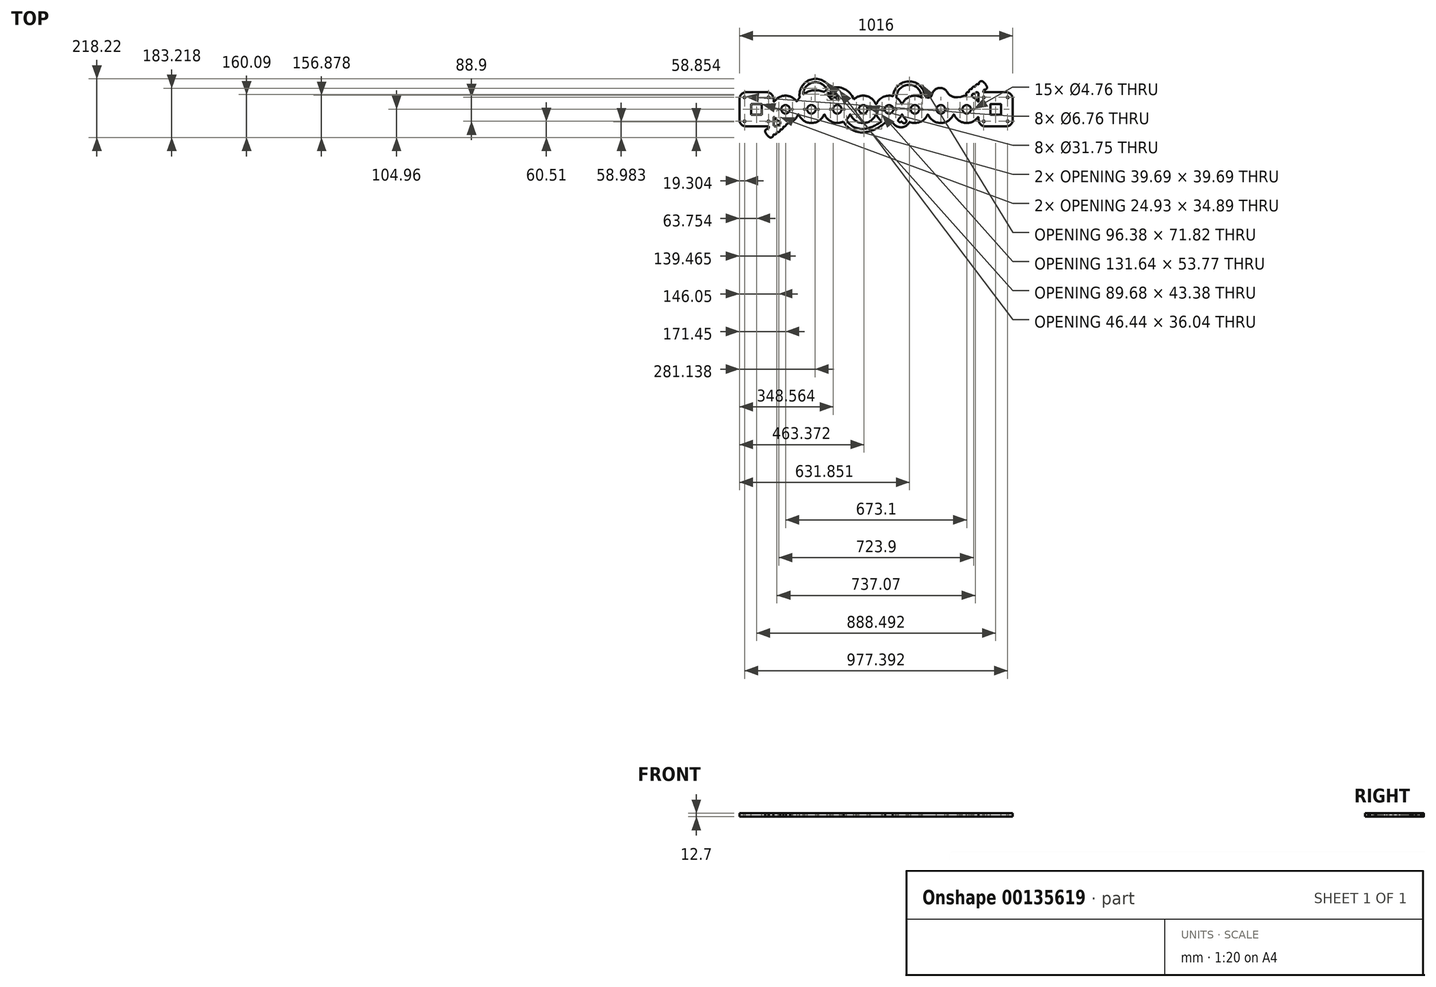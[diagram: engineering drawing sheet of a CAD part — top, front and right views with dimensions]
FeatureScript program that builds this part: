
annotation { "Feature Type Name" : "Feature", "Feature Type Description" : "" }
export const myFeature = defineFeature(function(context is Context, id is Id, definition is map)
    precondition{}
    {
        {
            var Q0;
            Q0=qCreatedBy(makeId("Top.planeOp"),FACE);
            var sketch = newSketch(context, id + "F0", { "sketchPlane" : qUnion([Q0])});
            skLineSegment(sketch, "E0", {"start": v(0, 0) * mm, "end": v(0, 330.74) * mm, "construction": true});
            skLineSegment(sketch, "E1.bottom", {"start": v(508, 63.5) * mm, "end": v(381, 63.5) * mm});
            skLineSegment(sketch, "E1.top", {"start": v(508, -63.5) * mm, "end": v(381, -63.5) * mm});
            skLineSegment(sketch, "E1.left", {"start": v(508, 63.5) * mm, "end": v(508, -63.5) * mm});
            skLineSegment(sketch, "E1.right", {"start": v(381, 63.5) * mm, "end": v(381, -63.5) * mm});
            skPoint(sketch, "E1.middle", {"position": v(444.5, 0) * mm});
            skPoint(sketch, "E2.MirrorP", {"position": v(-444.5, 0) * mm});
            skLineSegment(sketch, "E3.MirrorCS", {"start": v(-381, 63.5) * mm, "end": v(-381, -63.5) * mm});
            skLineSegment(sketch, "E4.MirrorCS", {"start": v(-508, 63.5) * mm, "end": v(-508, -63.5) * mm});
            skLineSegment(sketch, "E5.MirrorCS", {"start": v(-508, -63.5) * mm, "end": v(-381, -63.5) * mm});
            skLineSegment(sketch, "E6.MirrorCS", {"start": v(-508, 63.5) * mm, "end": v(-381, 63.5) * mm});
            skLineSegment(sketch, "E7", {"start": v(0, 0) * mm, "end": v(126.8, 0) * mm, "construction": true});
            skLineSegment(sketch, "E8.direction2", {"start": v(-381, -63.5) * mm, "end": v(-381, 63.5) * mm, "construction": true});
            skCircle(sketch, "E9", {"center": v(-336.55, 0) * mm, "radius": 50.8 * mm});
            skCircle(sketch, "E10.1.0.0", {"center": v(-240.4, 0) * mm, "radius": 50.8 * mm});
            skCircle(sketch, "E10.2.0.0", {"center": v(-144.24, 0) * mm, "radius": 50.8 * mm});
            skCircle(sketch, "E10.3.0.0", {"center": v(-48.08, 0) * mm, "radius": 50.8 * mm});
            skCircle(sketch, "E10.4.0.0", {"center": v(48.08, 0) * mm, "radius": 50.8 * mm});
            skCircle(sketch, "E10.5.0.0", {"center": v(144.24, 0) * mm, "radius": 50.8 * mm});
            skCircle(sketch, "E10.6.0.0", {"center": v(240.4, 0) * mm, "radius": 50.8 * mm});
            skCircle(sketch, "E10.7.0.0", {"center": v(336.55, 0) * mm, "radius": 50.8 * mm});
            skLineSegment(sketch, "E10.direction1", {"start": v(-336.55, 0) * mm, "end": v(-240.4, 0) * mm, "construction": true});
            skLineSegment(sketch, "E11", {"start": v(-381, 0) * mm, "end": v(-387.35, 0) * mm});
            skLineSegment(sketch, "E12", {"start": v(381, 0) * mm, "end": v(387.35, 0) * mm});
            skSolve(sketch);
        }
        {
            var Q0;
            Q0=qSketchRegion(id+"F0",true);
            extrude(context, id + "F1", {"entities" : qUnion([Q0]), "endBound" : BoundingType.SYMMETRIC, "depth" : 12.7 * mm});
        }
        {
            var Q0;
            Q0=makeQuery(id+"F1.opExtrude","SWEPT_EDGE",EDGE,{"disambiguationData":[OSD([sQuery(id+"F0.wireOp",EDGE,"E1.top"),sQuery(id+"F0.wireOp",EDGE,"E1.left")])]});
            var Q1;
            Q1=makeQuery(id+"F1.opExtrude","SWEPT_EDGE",EDGE,{"disambiguationData":[OSD([sQuery(id+"F0.wireOp",EDGE,"E1.top"),sQuery(id+"F0.wireOp",EDGE,"E1.right")])]});
            var Q2;
            Q2=makeQuery(id+"F1.opExtrude","SWEPT_EDGE",EDGE,{"disambiguationData":[OSD([sQuery(id+"F0.wireOp",EDGE,"E1.bottom"),sQuery(id+"F0.wireOp",EDGE,"E1.left")])]});
            var Q3;
            Q3=makeQuery(id+"F1.opExtrude","SWEPT_EDGE",EDGE,{"disambiguationData":[OSD([sQuery(id+"F0.wireOp",EDGE,"E4.MirrorCS"),sQuery(id+"F0.wireOp",EDGE,"E5.MirrorCS")])]});
            var Q4;
            Q4=makeQuery(id+"F1.opExtrude","SWEPT_EDGE",EDGE,{"disambiguationData":[OSD([sQuery(id+"F0.wireOp",EDGE,"E4.MirrorCS"),sQuery(id+"F0.wireOp",EDGE,"E6.MirrorCS")])]});
            var Q5;
            Q5=makeQuery(id+"F1.opExtrude","SWEPT_EDGE",EDGE,{"disambiguationData":[OSD([sQuery(id+"F0.wireOp",EDGE,"E3.MirrorCS"),sQuery(id+"F0.wireOp",EDGE,"E6.MirrorCS")])]});
            fillet(context, id + "F2", {"entities" : qUnion([Q0, Q1, Q2, Q3, Q4, Q5]), "radius" : 25.4 * mm, "tangentPropagation" : true, "allowEdgeOverflow" : false});
        }
        {
            var Q0;
            Q0=makeQuery(id+"F1.opExtrude","CAP_FACE",FACE,{"disambiguationData":[OSD([sQuery(id+"F0.wireOp",EDGE,"E1.bottom"),sQuery(id+"F0.wireOp",EDGE,"E1.top"),sQuery(id+"F0.wireOp",EDGE,"E1.left"),sQuery(id+"F0.wireOp",EDGE,"E1.right"),sQuery(id+"F0.wireOp",EDGE,"E3.MirrorCS"),sQuery(id+"F0.wireOp",EDGE,"E4.MirrorCS"),sQuery(id+"F0.wireOp",EDGE,"E5.MirrorCS"),sQuery(id+"F0.wireOp",EDGE,"E6.MirrorCS"),sQuery(id+"F0.wireOp",EDGE,"E9"),sQuery(id+"F0.wireOp",EDGE,"E10.1.0.0"),sQuery(id+"F0.wireOp",EDGE,"E10.2.0.0"),sQuery(id+"F0.wireOp",EDGE,"E10.3.0.0"),sQuery(id+"F0.wireOp",EDGE,"E10.4.0.0"),sQuery(id+"F0.wireOp",EDGE,"E10.5.0.0"),sQuery(id+"F0.wireOp",EDGE,"E10.6.0.0"),sQuery(id+"F0.wireOp",EDGE,"E10.7.0.0")])],"isStart":false});
            var sketch = newSketch(context, id + "F3", { "sketchPlane" : qUnion([Q0])});
            skArc(sketch, "E13", {"start": v(-381, -56.63) * mm, "mid": v(-374.13, -63.5) * mm, "end": v(-367.26, -56.63) * mm});
            skArc(sketch, "E14", {"start": v(-367.26, -56.63) * mm, "mid": v(-357.18, -55.03) * mm, "end": v(-359.8, -45.17) * mm});
            skArc(sketch, "E15", {"start": v(-347.92, -61.66) * mm, "mid": v(-336.63, -61.98) * mm, "end": v(-338.08, -50.78) * mm});
            skArc(sketch, "E16", {"start": v(-359.38, -71.23) * mm, "mid": v(-347.9, -73.34) * mm, "end": v(-347.92, -61.66) * mm});
            skArc(sketch, "E17", {"start": v(-369.91, -80.78) * mm, "mid": v(-358.7, -82.57) * mm, "end": v(-359.38, -71.23) * mm});
            skArc(sketch, "E18", {"start": v(-383, -91.32) * mm, "mid": v(-371.86, -91.75) * mm, "end": v(-369.91, -80.78) * mm});
            skArc(sketch, "E19", {"start": v(-397.93, -102.36) * mm, "mid": v(-385.83, -103.1) * mm, "end": v(-383, -91.32) * mm});
            skArc(sketch, "E20", {"start": v(-411.58, -84.76) * mm, "mid": v(-405.65, -94.26) * mm, "end": v(-397.93, -102.36) * mm});
            skArc(sketch, "E21", {"start": v(-399.42, -73.2) * mm, "mid": v(-409.27, -75) * mm, "end": v(-411.58, -84.76) * mm});
            skArc(sketch, "E22.0", {"start": v(-359.8, -45.17) * mm, "mid": v(-349.25, -49.19) * mm, "end": v(-338.08, -50.78) * mm});
            skLineSegment(sketch, "E23.0", {"start": v(-381, -56.63) * mm, "end": v(-381, -63.5) * mm});
            skLineSegment(sketch, "E24.0", {"start": v(-401.54, -63.5) * mm, "end": v(-381, -63.5) * mm});
            skPoint(sketch, "E25.orphan", {"position": v(-381, -24.6) * mm});
            skPoint(sketch, "E26.orphan", {"position": v(-482.6, -63.5) * mm});
            skPoint(sketch, "E27.orphan", {"position": v(-288.47, -16.4) * mm});
            skArc(sketch, "E28", {"start": v(-388.23, -65.24) * mm, "mid": v(-397.09, -64.64) * mm, "end": v(-399.42, -73.2) * mm});
            skCircle(sketch, "E29", {"center": v(0, 0) * mm, "radius": 77.09 * mm, "construction": true});
            skPoint(sketch, "E30.1.0", {"position": v(288.47, 16.4) * mm});
            skPoint(sketch, "E30.1.1", {"position": v(381, 24.6) * mm});
            skArc(sketch, "E30.1.2", {"start": v(383, 91.32) * mm, "mid": v(371.86, 91.75) * mm, "end": v(369.91, 80.78) * mm});
            skArc(sketch, "E30.1.3", {"start": v(359.38, 71.23) * mm, "mid": v(347.9, 73.34) * mm, "end": v(347.92, 61.66) * mm});
            skArc(sketch, "E30.1.4", {"start": v(347.92, 61.66) * mm, "mid": v(336.63, 61.98) * mm, "end": v(338.08, 50.78) * mm});
            skArc(sketch, "E30.1.5", {"start": v(397.93, 102.36) * mm, "mid": v(385.83, 103.1) * mm, "end": v(383, 91.32) * mm});
            skArc(sketch, "E30.1.6", {"start": v(411.58, 84.76) * mm, "mid": v(405.65, 94.26) * mm, "end": v(397.93, 102.36) * mm});
            skArc(sketch, "E30.1.7", {"start": v(359.8, 45.17) * mm, "mid": v(349.25, 49.19) * mm, "end": v(338.08, 50.78) * mm});
            skArc(sketch, "E30.1.8", {"start": v(369.91, 80.78) * mm, "mid": v(358.7, 82.57) * mm, "end": v(359.38, 71.23) * mm});
            skArc(sketch, "E30.1.9", {"start": v(367.26, 56.63) * mm, "mid": v(357.18, 55.03) * mm, "end": v(359.8, 45.17) * mm});
            skArc(sketch, "E30.1.10", {"start": v(399.42, 73.2) * mm, "mid": v(409.27, 75) * mm, "end": v(411.58, 84.76) * mm});
            skLineSegment(sketch, "E30.1.11", {"start": v(401.54, 63.5) * mm, "end": v(381, 63.5) * mm});
            skArc(sketch, "E30.1.12", {"start": v(388.23, 65.24) * mm, "mid": v(397.09, 64.64) * mm, "end": v(399.42, 73.2) * mm});
            skLineSegment(sketch, "E30.1.13", {"start": v(381, 56.63) * mm, "end": v(381, 63.5) * mm});
            skArc(sketch, "E30.1.14", {"start": v(381, 56.63) * mm, "mid": v(374.13, 63.5) * mm, "end": v(367.26, 56.63) * mm});
            skSolve(sketch);
        }
        {
            var Q0;
            Q0 = qSketchRegion(id + "F3", true);
            var Q1;
            Q1=makeQuery(id+"F1.opExtrude","CAP_FACE",FACE,{"disambiguationData":[OSD([sQuery(id+"F0.wireOp",EDGE,"E1.bottom"),sQuery(id+"F0.wireOp",EDGE,"E1.top"),sQuery(id+"F0.wireOp",EDGE,"E1.left"),sQuery(id+"F0.wireOp",EDGE,"E1.right"),sQuery(id+"F0.wireOp",EDGE,"E3.MirrorCS"),sQuery(id+"F0.wireOp",EDGE,"E4.MirrorCS"),sQuery(id+"F0.wireOp",EDGE,"E5.MirrorCS"),sQuery(id+"F0.wireOp",EDGE,"E6.MirrorCS"),sQuery(id+"F0.wireOp",EDGE,"E9"),sQuery(id+"F0.wireOp",EDGE,"E10.1.0.0"),sQuery(id+"F0.wireOp",EDGE,"E10.2.0.0"),sQuery(id+"F0.wireOp",EDGE,"E10.3.0.0"),sQuery(id+"F0.wireOp",EDGE,"E10.4.0.0"),sQuery(id+"F0.wireOp",EDGE,"E10.5.0.0"),sQuery(id+"F0.wireOp",EDGE,"E10.6.0.0"),sQuery(id+"F0.wireOp",EDGE,"E10.7.0.0")])],"isStart":true});
            extrude(context, id + "F4", {"entities" : qUnion([Q0]), "operationType" : NewBodyOperationType.ADD, "endBound" : BoundingType.UP_TO_SURFACE, "oppositeDirection" : true, "endBoundEntityFace" : qUnion([Q1]), "depth" : 25.4 * mm});
        }
        {
            var Q0;
            Q0=makeQuery(id+"F4.boolean.opBoolean","MERGE",FACE,{"derivedFrom":[makeQuery(id+"F1.opExtrude","CAP_FACE",FACE,{"disambiguationData":[OSD([sQuery(id+"F0.wireOp",EDGE,"E1.bottom"),sQuery(id+"F0.wireOp",EDGE,"E1.top"),sQuery(id+"F0.wireOp",EDGE,"E1.left"),sQuery(id+"F0.wireOp",EDGE,"E1.right"),sQuery(id+"F0.wireOp",EDGE,"E3.MirrorCS"),sQuery(id+"F0.wireOp",EDGE,"E4.MirrorCS"),sQuery(id+"F0.wireOp",EDGE,"E5.MirrorCS"),sQuery(id+"F0.wireOp",EDGE,"E6.MirrorCS"),sQuery(id+"F0.wireOp",EDGE,"E9"),sQuery(id+"F0.wireOp",EDGE,"E10.1.0.0"),sQuery(id+"F0.wireOp",EDGE,"E10.2.0.0"),sQuery(id+"F0.wireOp",EDGE,"E10.3.0.0"),sQuery(id+"F0.wireOp",EDGE,"E10.4.0.0"),sQuery(id+"F0.wireOp",EDGE,"E10.5.0.0"),sQuery(id+"F0.wireOp",EDGE,"E10.6.0.0"),sQuery(id+"F0.wireOp",EDGE,"E10.7.0.0")])],"isStart":false}),makeQuery(id+"F4.opExtrude","CAP_FACE",FACE,{"disambiguationData":[OSD([sQuery(id+"F3.wireOp",EDGE,"E13"),sQuery(id+"F3.wireOp",EDGE,"E14"),sQuery(id+"F3.wireOp",EDGE,"E15"),sQuery(id+"F3.wireOp",EDGE,"E16"),sQuery(id+"F3.wireOp",EDGE,"E17"),sQuery(id+"F3.wireOp",EDGE,"E18"),sQuery(id+"F3.wireOp",EDGE,"E19"),sQuery(id+"F3.wireOp",EDGE,"E20"),sQuery(id+"F3.wireOp",EDGE,"E21"),sQuery(id+"F3.wireOp",EDGE,"E22.0"),sQuery(id+"F3.wireOp",EDGE,"E23.0"),sQuery(id+"F3.wireOp",EDGE,"E24.0"),sQuery(id+"F3.wireOp",EDGE,"E28")])],"isStart":true}),makeQuery(id+"F4.opExtrude","CAP_FACE",FACE,{"disambiguationData":[OSD([sQuery(id+"F3.wireOp",EDGE,"E30.1.2"),sQuery(id+"F3.wireOp",EDGE,"E30.1.3"),sQuery(id+"F3.wireOp",EDGE,"E30.1.4"),sQuery(id+"F3.wireOp",EDGE,"E30.1.5"),sQuery(id+"F3.wireOp",EDGE,"E30.1.6"),sQuery(id+"F3.wireOp",EDGE,"E30.1.7"),sQuery(id+"F3.wireOp",EDGE,"E30.1.8"),sQuery(id+"F3.wireOp",EDGE,"E30.1.9"),sQuery(id+"F3.wireOp",EDGE,"E30.1.10"),sQuery(id+"F3.wireOp",EDGE,"E30.1.11"),sQuery(id+"F3.wireOp",EDGE,"E30.1.12"),sQuery(id+"F3.wireOp",EDGE,"E30.1.13"),sQuery(id+"F3.wireOp",EDGE,"E30.1.14")])],"isStart":true})]});
            var sketch = newSketch(context, id + "F5", { "sketchPlane" : qUnion([Q0])});
            skArc(sketch, "E31", {"start": v(-82.98, 36.91) * mm, "mid": v(-130.84, 79.98) * mm, "end": v(-193.32, 64.4) * mm});
            skArc(sketch, "E32", {"start": v(-193.32, 64.4) * mm, "mid": v(-250.9, 66.18) * mm, "end": v(-294.48, 28.47) * mm});
            skArc(sketch, "E33.0", {"start": v(-96.16, 16.4) * mm, "mid": v(-144.24, 50.8) * mm, "end": v(-192.31, 16.4) * mm});
            skArc(sketch, "E34.0", {"start": v(-192.31, 16.4) * mm, "mid": v(-240.4, 50.8) * mm, "end": v(-288.47, 16.4) * mm});
            skArc(sketch, "E35.0", {"start": v(-82.98, 36.91) * mm, "mid": v(-90.82, 27.46) * mm, "end": v(-96.16, 16.4) * mm});
            skArc(sketch, "E36.0", {"start": v(-288.47, 16.4) * mm, "mid": v(-291.07, 22.64) * mm, "end": v(-294.48, 28.47) * mm});
            skPoint(sketch, "E37.orphan", {"position": v(0, 16.4) * mm});
            skPoint(sketch, "E38.orphan", {"position": v(-381, 24.6) * mm});
            skSolve(sketch);
        }
        {
            var Q0;
            Q0 = qSketchRegion(id + "F5", true);
            var Q1;
            {var subQ0=sQuery(id+"F0.wireOp",EDGE,"E10.7.0.0");var subQ1=sQuery(id+"F0.wireOp",EDGE,"E10.6.0.0");var subQ2=sQuery(id+"F0.wireOp",EDGE,"E10.5.0.0");var subQ3=sQuery(id+"F0.wireOp",EDGE,"E10.4.0.0");var subQ4=sQuery(id+"F0.wireOp",EDGE,"E10.3.0.0");var subQ5=sQuery(id+"F0.wireOp",EDGE,"E10.2.0.0");var subQ6=sQuery(id+"F0.wireOp",EDGE,"E10.1.0.0");var subQ7=sQuery(id+"F0.wireOp",EDGE,"E9");var subQ8=sQuery(id+"F0.wireOp",EDGE,"E6.MirrorCS");var subQ9=sQuery(id+"F0.wireOp",EDGE,"E5.MirrorCS");var subQ10=sQuery(id+"F0.wireOp",EDGE,"E4.MirrorCS");var subQ11=sQuery(id+"F0.wireOp",EDGE,"E3.MirrorCS");var subQ12=sQuery(id+"F0.wireOp",EDGE,"E1.right");var subQ13=sQuery(id+"F0.wireOp",EDGE,"E1.left");var subQ14=sQuery(id+"F0.wireOp",EDGE,"E1.top");var subQ15=sQuery(id+"F0.wireOp",EDGE,"E1.bottom");Q1=makeQuery(id+"F4.boolean.opBoolean","MERGE",FACE,{"derivedFrom":[makeQuery(id+"F1.opExtrude","CAP_FACE",FACE,{"disambiguationData":[OSD([subQ15,subQ14,subQ13,subQ12,subQ11,subQ10,subQ9,subQ8,subQ7,subQ6,subQ5,subQ4,subQ3,subQ2,subQ1,subQ0])],"isStart":true}),makeQuery(id+"F4.opExtrude","CAP_FACE",FACE,{"disambiguationData":[OSD([subQ15,subQ14,subQ13,subQ12,subQ11,subQ10,subQ9,subQ8,subQ7,subQ6,subQ5,subQ4,subQ3,subQ2,subQ1,subQ0]),ownerDisambiguation([makeQuery(id+"F4.opExtrude","SWEPT_BODY",BODY,{"disambiguationData":[OSD([sQuery(id+"F3.wireOp",EDGE,"E13"),sQuery(id+"F3.wireOp",EDGE,"E14"),sQuery(id+"F3.wireOp",EDGE,"E15"),sQuery(id+"F3.wireOp",EDGE,"E16"),sQuery(id+"F3.wireOp",EDGE,"E17"),sQuery(id+"F3.wireOp",EDGE,"E18"),sQuery(id+"F3.wireOp",EDGE,"E19"),sQuery(id+"F3.wireOp",EDGE,"E20"),sQuery(id+"F3.wireOp",EDGE,"E21"),sQuery(id+"F3.wireOp",EDGE,"E22.0"),sQuery(id+"F3.wireOp",EDGE,"E23.0"),sQuery(id+"F3.wireOp",EDGE,"E24.0"),sQuery(id+"F3.wireOp",EDGE,"E28")])]})])],"isStart":false}),makeQuery(id+"F4.opExtrude","CAP_FACE",FACE,{"disambiguationData":[OSD([subQ15,subQ14,subQ13,subQ12,subQ11,subQ10,subQ9,subQ8,subQ7,subQ6,subQ5,subQ4,subQ3,subQ2,subQ1,subQ0]),ownerDisambiguation([makeQuery(id+"F4.opExtrude","SWEPT_BODY",BODY,{"disambiguationData":[OSD([sQuery(id+"F3.wireOp",EDGE,"E30.1.2"),sQuery(id+"F3.wireOp",EDGE,"E30.1.3"),sQuery(id+"F3.wireOp",EDGE,"E30.1.4"),sQuery(id+"F3.wireOp",EDGE,"E30.1.5"),sQuery(id+"F3.wireOp",EDGE,"E30.1.6"),sQuery(id+"F3.wireOp",EDGE,"E30.1.7"),sQuery(id+"F3.wireOp",EDGE,"E30.1.8"),sQuery(id+"F3.wireOp",EDGE,"E30.1.9"),sQuery(id+"F3.wireOp",EDGE,"E30.1.10"),sQuery(id+"F3.wireOp",EDGE,"E30.1.11"),sQuery(id+"F3.wireOp",EDGE,"E30.1.12"),sQuery(id+"F3.wireOp",EDGE,"E30.1.13"),sQuery(id+"F3.wireOp",EDGE,"E30.1.14")])]})])],"isStart":false})]});}
            extrude(context, id + "F6", {"entities" : qUnion([Q0]), "operationType" : NewBodyOperationType.ADD, "endBound" : BoundingType.UP_TO_SURFACE, "oppositeDirection" : true, "endBoundEntityFace" : qUnion([Q1]), "depth" : 25.4 * mm});
        }
        {
            var Q0;
            Q0=makeQuery(id+"F6.boolean.opBoolean","MERGE",FACE,{"derivedFrom":[makeQuery(id+"F4.boolean.opBoolean","MERGE",FACE,{"derivedFrom":[makeQuery(id+"F1.opExtrude","CAP_FACE",FACE,{"disambiguationData":[OSD([sQuery(id+"F0.wireOp",EDGE,"E1.bottom"),sQuery(id+"F0.wireOp",EDGE,"E1.top"),sQuery(id+"F0.wireOp",EDGE,"E1.left"),sQuery(id+"F0.wireOp",EDGE,"E1.right"),sQuery(id+"F0.wireOp",EDGE,"E3.MirrorCS"),sQuery(id+"F0.wireOp",EDGE,"E4.MirrorCS"),sQuery(id+"F0.wireOp",EDGE,"E5.MirrorCS"),sQuery(id+"F0.wireOp",EDGE,"E6.MirrorCS"),sQuery(id+"F0.wireOp",EDGE,"E9"),sQuery(id+"F0.wireOp",EDGE,"E10.1.0.0"),sQuery(id+"F0.wireOp",EDGE,"E10.2.0.0"),sQuery(id+"F0.wireOp",EDGE,"E10.3.0.0"),sQuery(id+"F0.wireOp",EDGE,"E10.4.0.0"),sQuery(id+"F0.wireOp",EDGE,"E10.5.0.0"),sQuery(id+"F0.wireOp",EDGE,"E10.6.0.0"),sQuery(id+"F0.wireOp",EDGE,"E10.7.0.0")])],"isStart":false}),makeQuery(id+"F4.opExtrude","CAP_FACE",FACE,{"disambiguationData":[OSD([sQuery(id+"F3.wireOp",EDGE,"E13"),sQuery(id+"F3.wireOp",EDGE,"E14"),sQuery(id+"F3.wireOp",EDGE,"E15"),sQuery(id+"F3.wireOp",EDGE,"E16"),sQuery(id+"F3.wireOp",EDGE,"E17"),sQuery(id+"F3.wireOp",EDGE,"E18"),sQuery(id+"F3.wireOp",EDGE,"E19"),sQuery(id+"F3.wireOp",EDGE,"E20"),sQuery(id+"F3.wireOp",EDGE,"E21"),sQuery(id+"F3.wireOp",EDGE,"E22.0"),sQuery(id+"F3.wireOp",EDGE,"E23.0"),sQuery(id+"F3.wireOp",EDGE,"E24.0"),sQuery(id+"F3.wireOp",EDGE,"E28")])],"isStart":true}),makeQuery(id+"F4.opExtrude","CAP_FACE",FACE,{"disambiguationData":[OSD([sQuery(id+"F3.wireOp",EDGE,"E30.1.2"),sQuery(id+"F3.wireOp",EDGE,"E30.1.3"),sQuery(id+"F3.wireOp",EDGE,"E30.1.4"),sQuery(id+"F3.wireOp",EDGE,"E30.1.5"),sQuery(id+"F3.wireOp",EDGE,"E30.1.6"),sQuery(id+"F3.wireOp",EDGE,"E30.1.7"),sQuery(id+"F3.wireOp",EDGE,"E30.1.8"),sQuery(id+"F3.wireOp",EDGE,"E30.1.9"),sQuery(id+"F3.wireOp",EDGE,"E30.1.10"),sQuery(id+"F3.wireOp",EDGE,"E30.1.11"),sQuery(id+"F3.wireOp",EDGE,"E30.1.12"),sQuery(id+"F3.wireOp",EDGE,"E30.1.13"),sQuery(id+"F3.wireOp",EDGE,"E30.1.14")])],"isStart":true})]}),makeQuery(id+"F6.opExtrude","CAP_FACE",FACE,{"disambiguationData":[OSD([sQuery(id+"F5.wireOp",EDGE,"E31"),sQuery(id+"F5.wireOp",EDGE,"E32"),sQuery(id+"F5.wireOp",EDGE,"E33.0"),sQuery(id+"F5.wireOp",EDGE,"E34.0"),sQuery(id+"F5.wireOp",EDGE,"E35.0"),sQuery(id+"F5.wireOp",EDGE,"E36.0")])],"isStart":true})]});
            var sketch = newSketch(context, id + "F7", { "sketchPlane" : qUnion([Q0])});
            skArc(sketch, "E39", {"start": v(84.14, -35.78) * mm, "mid": v(85.22, -46.67) * mm, "end": v(95.4, -42.66) * mm});
            skArc(sketch, "E40", {"start": v(95.4, -42.66) * mm, "mid": v(105.84, -51.57) * mm, "end": v(112.13, -39.37) * mm});
            skArc(sketch, "E41", {"start": v(61.74, -48.93) * mm, "mid": v(93.64, -66.78) * mm, "end": v(124.18, -46.67) * mm});
            skPoint(sketch, "E41.endSnap0", {"position": v(85.22, -46.67) * mm});
            skArc(sketch, "E42.0", {"start": v(61.74, -48.93) * mm, "mid": v(73.8, -43.81) * mm, "end": v(84.14, -35.78) * mm});
            skPoint(sketch, "E43.orphan", {"position": v(0, -16.4) * mm});
            skPoint(sketch, "E44.orphan", {"position": v(192.31, -16.4) * mm});
            skPoint(sketch, "E45.orphan", {"position": v(96.16, -16.4) * mm});
            skSolve(sketch);
        }
        {
            var Q0;
            Q0 = qSketchRegion(id + "F7", true);
            var Q1;
            {var subQ0=sQuery(id+"F7.wireOp",EDGE,"E40");Q1=makeQuery(id+"F7.imprint","IMPRINT",FACE,{"disambiguationData":[TD([[makeQuery(id+"F7.imprint","IMPRINT",EDGE,{"derivedFrom":subQ0}),-1.0]])]});}
            var Q2;
            {var subQ0=sQuery(id+"F0.wireOp",EDGE,"E10.7.0.0");var subQ1=sQuery(id+"F0.wireOp",EDGE,"E10.6.0.0");var subQ2=sQuery(id+"F0.wireOp",EDGE,"E10.5.0.0");var subQ3=sQuery(id+"F0.wireOp",EDGE,"E10.4.0.0");var subQ4=sQuery(id+"F0.wireOp",EDGE,"E10.3.0.0");var subQ5=sQuery(id+"F0.wireOp",EDGE,"E10.2.0.0");var subQ6=sQuery(id+"F0.wireOp",EDGE,"E10.1.0.0");var subQ7=sQuery(id+"F0.wireOp",EDGE,"E9");var subQ8=sQuery(id+"F0.wireOp",EDGE,"E6.MirrorCS");var subQ9=sQuery(id+"F0.wireOp",EDGE,"E5.MirrorCS");var subQ10=sQuery(id+"F0.wireOp",EDGE,"E4.MirrorCS");var subQ11=sQuery(id+"F0.wireOp",EDGE,"E3.MirrorCS");var subQ12=sQuery(id+"F0.wireOp",EDGE,"E1.right");var subQ13=sQuery(id+"F0.wireOp",EDGE,"E1.left");var subQ14=sQuery(id+"F0.wireOp",EDGE,"E1.top");var subQ15=sQuery(id+"F0.wireOp",EDGE,"E1.bottom");Q2=makeQuery(id+"F6.boolean.opBoolean","MERGE",FACE,{"derivedFrom":[makeQuery(id+"F4.boolean.opBoolean","MERGE",FACE,{"derivedFrom":[makeQuery(id+"F1.opExtrude","CAP_FACE",FACE,{"disambiguationData":[OSD([subQ15,subQ14,subQ13,subQ12,subQ11,subQ10,subQ9,subQ8,subQ7,subQ6,subQ5,subQ4,subQ3,subQ2,subQ1,subQ0])],"isStart":true}),makeQuery(id+"F4.opExtrude","CAP_FACE",FACE,{"disambiguationData":[OSD([subQ15,subQ14,subQ13,subQ12,subQ11,subQ10,subQ9,subQ8,subQ7,subQ6,subQ5,subQ4,subQ3,subQ2,subQ1,subQ0]),ownerDisambiguation([makeQuery(id+"F4.opExtrude","SWEPT_BODY",BODY,{"disambiguationData":[OSD([sQuery(id+"F3.wireOp",EDGE,"E13"),sQuery(id+"F3.wireOp",EDGE,"E14"),sQuery(id+"F3.wireOp",EDGE,"E15"),sQuery(id+"F3.wireOp",EDGE,"E16"),sQuery(id+"F3.wireOp",EDGE,"E17"),sQuery(id+"F3.wireOp",EDGE,"E18"),sQuery(id+"F3.wireOp",EDGE,"E19"),sQuery(id+"F3.wireOp",EDGE,"E20"),sQuery(id+"F3.wireOp",EDGE,"E21"),sQuery(id+"F3.wireOp",EDGE,"E22.0"),sQuery(id+"F3.wireOp",EDGE,"E23.0"),sQuery(id+"F3.wireOp",EDGE,"E24.0"),sQuery(id+"F3.wireOp",EDGE,"E28")])]})])],"isStart":false}),makeQuery(id+"F4.opExtrude","CAP_FACE",FACE,{"disambiguationData":[OSD([subQ15,subQ14,subQ13,subQ12,subQ11,subQ10,subQ9,subQ8,subQ7,subQ6,subQ5,subQ4,subQ3,subQ2,subQ1,subQ0]),ownerDisambiguation([makeQuery(id+"F4.opExtrude","SWEPT_BODY",BODY,{"disambiguationData":[OSD([sQuery(id+"F3.wireOp",EDGE,"E30.1.2"),sQuery(id+"F3.wireOp",EDGE,"E30.1.3"),sQuery(id+"F3.wireOp",EDGE,"E30.1.4"),sQuery(id+"F3.wireOp",EDGE,"E30.1.5"),sQuery(id+"F3.wireOp",EDGE,"E30.1.6"),sQuery(id+"F3.wireOp",EDGE,"E30.1.7"),sQuery(id+"F3.wireOp",EDGE,"E30.1.8"),sQuery(id+"F3.wireOp",EDGE,"E30.1.9"),sQuery(id+"F3.wireOp",EDGE,"E30.1.10"),sQuery(id+"F3.wireOp",EDGE,"E30.1.11"),sQuery(id+"F3.wireOp",EDGE,"E30.1.12"),sQuery(id+"F3.wireOp",EDGE,"E30.1.13"),sQuery(id+"F3.wireOp",EDGE,"E30.1.14")])]})])],"isStart":false})]}),makeQuery(id+"F6.opExtrude","CAP_FACE",FACE,{"disambiguationData":[OSD([subQ15,subQ14,subQ13,subQ12,subQ11,subQ10,subQ9,subQ8,subQ7,subQ6,subQ5,subQ4,subQ3,subQ2,subQ1,subQ0])],"isStart":false})]});}
            extrude(context, id + "F8", {"entities" : qUnion([Q0, Q1]), "operationType" : NewBodyOperationType.ADD, "endBound" : BoundingType.UP_TO_SURFACE, "oppositeDirection" : true, "endBoundEntityFace" : qUnion([Q2]), "depth" : 25.4 * mm});
        }
        {
            var Q0;
            {var subQ0=sQuery(id+"F0.wireOp",EDGE,"E10.5.0.0");Q0=makeQuery(id+"F8.boolean.opBoolean","MERGE",FACE,{"derivedFrom":[makeQuery(id+"F6.boolean.opBoolean","MERGE",FACE,{"derivedFrom":[makeQuery(id+"F4.boolean.opBoolean","MERGE",FACE,{"derivedFrom":[makeQuery(id+"F1.opExtrude","CAP_FACE",FACE,{"disambiguationData":[OSD([sQuery(id+"F0.wireOp",EDGE,"E1.bottom"),sQuery(id+"F0.wireOp",EDGE,"E1.top"),sQuery(id+"F0.wireOp",EDGE,"E1.left"),sQuery(id+"F0.wireOp",EDGE,"E1.right"),sQuery(id+"F0.wireOp",EDGE,"E3.MirrorCS"),sQuery(id+"F0.wireOp",EDGE,"E4.MirrorCS"),sQuery(id+"F0.wireOp",EDGE,"E5.MirrorCS"),sQuery(id+"F0.wireOp",EDGE,"E6.MirrorCS"),sQuery(id+"F0.wireOp",EDGE,"E9"),sQuery(id+"F0.wireOp",EDGE,"E10.1.0.0"),sQuery(id+"F0.wireOp",EDGE,"E10.2.0.0"),sQuery(id+"F0.wireOp",EDGE,"E10.3.0.0"),sQuery(id+"F0.wireOp",EDGE,"E10.4.0.0"),subQ0,sQuery(id+"F0.wireOp",EDGE,"E10.6.0.0"),sQuery(id+"F0.wireOp",EDGE,"E10.7.0.0")])],"isStart":false}),makeQuery(id+"F4.opExtrude","CAP_FACE",FACE,{"disambiguationData":[OSD([sQuery(id+"F3.wireOp",EDGE,"E13"),sQuery(id+"F3.wireOp",EDGE,"E14"),sQuery(id+"F3.wireOp",EDGE,"E15"),sQuery(id+"F3.wireOp",EDGE,"E16"),sQuery(id+"F3.wireOp",EDGE,"E17"),sQuery(id+"F3.wireOp",EDGE,"E18"),sQuery(id+"F3.wireOp",EDGE,"E19"),sQuery(id+"F3.wireOp",EDGE,"E20"),sQuery(id+"F3.wireOp",EDGE,"E21"),sQuery(id+"F3.wireOp",EDGE,"E22.0"),sQuery(id+"F3.wireOp",EDGE,"E23.0"),sQuery(id+"F3.wireOp",EDGE,"E24.0"),sQuery(id+"F3.wireOp",EDGE,"E28")])],"isStart":true}),makeQuery(id+"F4.opExtrude","CAP_FACE",FACE,{"disambiguationData":[OSD([sQuery(id+"F3.wireOp",EDGE,"E30.1.2"),sQuery(id+"F3.wireOp",EDGE,"E30.1.3"),sQuery(id+"F3.wireOp",EDGE,"E30.1.4"),sQuery(id+"F3.wireOp",EDGE,"E30.1.5"),sQuery(id+"F3.wireOp",EDGE,"E30.1.6"),sQuery(id+"F3.wireOp",EDGE,"E30.1.7"),sQuery(id+"F3.wireOp",EDGE,"E30.1.8"),sQuery(id+"F3.wireOp",EDGE,"E30.1.9"),sQuery(id+"F3.wireOp",EDGE,"E30.1.10"),sQuery(id+"F3.wireOp",EDGE,"E30.1.11"),sQuery(id+"F3.wireOp",EDGE,"E30.1.12"),sQuery(id+"F3.wireOp",EDGE,"E30.1.13"),sQuery(id+"F3.wireOp",EDGE,"E30.1.14")])],"isStart":true})]}),makeQuery(id+"F6.opExtrude","CAP_FACE",FACE,{"disambiguationData":[OSD([sQuery(id+"F5.wireOp",EDGE,"E31"),sQuery(id+"F5.wireOp",EDGE,"E32"),sQuery(id+"F5.wireOp",EDGE,"E33.0"),sQuery(id+"F5.wireOp",EDGE,"E34.0"),sQuery(id+"F5.wireOp",EDGE,"E35.0"),sQuery(id+"F5.wireOp",EDGE,"E36.0")])],"isStart":true})]}),makeQuery(id+"F8.opExtrude","CAP_FACE",FACE,{"disambiguationData":[OSD([subQ0,sQuery(id+"F7.wireOp",EDGE,"E39"),sQuery(id+"F7.wireOp",EDGE,"E40"),sQuery(id+"F7.wireOp",EDGE,"E41"),sQuery(id+"F7.wireOp",EDGE,"E42.0")])],"isStart":true})]});}
            var sketch = newSketch(context, id + "F9", { "sketchPlane" : qUnion([Q0])});
            skArc(sketch, "E46", {"start": v(-338.08, -50.78) * mm, "mid": v(-292.29, -9.96) * mm, "end": v(-278.15, 49.72) * mm, "construction": true});
            skArc(sketch, "E47", {"start": v(-176.39, 75.6) * mm, "mid": v(-238.1, 105.27) * mm, "end": v(-278.15, 49.72) * mm, "construction": true});
            skArc(sketch, "E48", {"start": v(-176.39, 75.6) * mm, "mid": v(-147.6, 15.97) * mm, "end": v(-115.97, -42.2) * mm, "construction": true});
            skArc(sketch, "E49", {"start": v(-115.97, -42.2) * mm, "mid": v(-84, -71.95) * mm, "end": v(-40.84, -78.54) * mm, "construction": true});
            skArc(sketch, "E50", {"start": v(-40.84, -78.54) * mm, "mid": v(37, -36.31) * mm, "end": v(69.44, 46.1) * mm, "construction": true});
            skArc(sketch, "E51", {"start": v(174.2, 53.82) * mm, "mid": v(118.32, 97.37) * mm, "end": v(69.44, 46.1) * mm, "construction": true});
            skArc(sketch, "E52", {"start": v(174.2, 53.82) * mm, "mid": v(193.83, 37.14) * mm, "end": v(213.8, 53.42) * mm, "construction": true});
            skArc(sketch, "E53", {"start": v(258.8, 88.1) * mm, "mid": v(258.72, 88.1) * mm, "end": v(258.65, 88.1) * mm});
            skArc(sketch, "E54", {"start": v(258.77, 60.59) * mm, "mid": v(233.78, 72.72) * mm, "end": v(213.8, 53.42) * mm, "construction": true});
            skArc(sketch, "E55", {"start": v(258.77, 60.59) * mm, "mid": v(277.96, 42.6) * mm, "end": v(304.01, 39.01) * mm, "construction": true});
            skArc(sketch, "E56.0", {"start": v(253.23, 57.5) * mm, "mid": v(275.22, 36.86) * mm, "end": v(305.1, 32.76) * mm});
            skArc(sketch, "E56.1", {"start": v(253.23, 57.5) * mm, "mid": v(234.78, 66.45) * mm, "end": v(220.03, 52.2) * mm});
            skArc(sketch, "E56.2", {"start": v(167.94, 52.73) * mm, "mid": v(193.77, 30.8) * mm, "end": v(220.03, 52.2) * mm});
            skArc(sketch, "E56.3", {"start": v(167.94, 52.73) * mm, "mid": v(118.78, 91.04) * mm, "end": v(75.78, 45.93) * mm});
            skArc(sketch, "E56.4", {"start": v(-39.91, -84.82) * mm, "mid": v(41.75, -40.52) * mm, "end": v(75.78, 45.93) * mm});
            skArc(sketch, "E56.5", {"start": v(-335.47, -56.57) * mm, "mid": v(-286.83, -13.22) * mm, "end": v(-271.82, 50.18) * mm});
            skArc(sketch, "E56.6", {"start": v(-182.17, 72.98) * mm, "mid": v(-236.54, 99.12) * mm, "end": v(-271.82, 50.18) * mm});
            skArc(sketch, "E56.7", {"start": v(-182.17, 72.98) * mm, "mid": v(-153.25, 13.07) * mm, "end": v(-121.47, -45.37) * mm});
            skArc(sketch, "E56.8", {"start": v(-121.47, -45.37) * mm, "mid": v(-86.77, -77.67) * mm, "end": v(-39.91, -84.82) * mm});
            skArc(sketch, "E57.0", {"start": v(264.32, 63.68) * mm, "mid": v(280.69, 48.32) * mm, "end": v(302.93, 45.27) * mm});
            skArc(sketch, "E57.1", {"start": v(264.32, 63.68) * mm, "mid": v(232.79, 79) * mm, "end": v(207.57, 54.64) * mm});
            skArc(sketch, "E57.2", {"start": v(180.45, 54.91) * mm, "mid": v(193.9, 43.5) * mm, "end": v(207.57, 54.64) * mm});
            skArc(sketch, "E57.3", {"start": v(180.45, 54.91) * mm, "mid": v(117.85, 103.7) * mm, "end": v(63.09, 46.25) * mm});
            skArc(sketch, "E57.4", {"start": v(-41.78, -72.26) * mm, "mid": v(32.24, -32.1) * mm, "end": v(63.09, 46.25) * mm});
            skArc(sketch, "E57.5", {"start": v(-340.68, -44.99) * mm, "mid": v(-297.74, -6.71) * mm, "end": v(-284.48, 49.26) * mm});
            skArc(sketch, "E57.6", {"start": v(-170.6, 78.22) * mm, "mid": v(-239.67, 111.42) * mm, "end": v(-284.48, 49.26) * mm});
            skArc(sketch, "E57.7", {"start": v(-170.6, 78.22) * mm, "mid": v(-141.95, 18.87) * mm, "end": v(-110.46, -39.04) * mm});
            skArc(sketch, "E57.8", {"start": v(-110.46, -39.04) * mm, "mid": v(-81.24, -66.24) * mm, "end": v(-41.78, -72.26) * mm});
            skLineSegment(sketch, "E58", {"start": v(-340.83, -45.13) * mm, "end": v(-335.47, -56.57) * mm});
            skLineSegment(sketch, "E59", {"start": v(302.93, 45.27) * mm, "end": v(315.97, 46.45) * mm});
            skLineSegment(sketch, "E60", {"start": v(315.97, 46.45) * mm, "end": v(305.1, 32.76) * mm});
            skArc(sketch, "E61.0", {"start": v(192.31, 16.4) * mm, "mid": v(144.24, 50.8) * mm, "end": v(96.16, 16.4) * mm});
            skArc(sketch, "E62.0", {"start": v(338.08, 50.78) * mm, "mid": v(307.62, 41.76) * mm, "end": v(288.47, 16.4) * mm});
            skArc(sketch, "E63.0", {"start": v(288.47, 16.4) * mm, "mid": v(240.4, 50.8) * mm, "end": v(192.31, 16.4) * mm});
            skSolve(sketch);
        }
        {
            var Q0;
            {var subQ0=sQuery(id+"F9.wireOp",EDGE,"E57.6");Q0=makeQuery(id+"F9.imprint","IMPRINT",FACE,{"disambiguationData":[TD([[makeQuery(id+"F9.imprint","IMPRINT",EDGE,{"derivedFrom":subQ0}),1.0]])]});}
            var Q1;
            {var subQ0=sQuery(id+"F9.wireOp",EDGE,"E56.5");var subQ1=sQuery(id+"F3.wireOp",EDGE,"E15");var subQ2=makeQuery(id+"F4.opExtrude","CAP_EDGE",EDGE,{"disambiguationData":[OSD([subQ1])],"isStart":true});var subQ3=makeQuery(id+"F9.imprint","INTERSECT",VERTEX,{"derivedFrom":[subQ2,subQ0]});Q1=makeQuery(id+"F9.imprint","IMPRINT",FACE,{"disambiguationData":[TD([[makeQuery(id+"F9.imprint","IMPRINT",EDGE,{"disambiguationData":[TD([[subQ3,-1.0]])],"derivedFrom":subQ0}),1.0]])]});}
            var Q2;
            {var subQ0=sQuery(id+"F9.wireOp",EDGE,"E57.8");Q2=makeQuery(id+"F9.imprint","IMPRINT",FACE,{"disambiguationData":[TD([[makeQuery(id+"F9.imprint","IMPRINT",EDGE,{"derivedFrom":subQ0}),-1.0]])]});}
            var Q3;
            {var subQ23=sQuery(id+"F9.wireOp",EDGE,"E56.1");Q3=makeQuery(id+"F9.imprint","IMPRINT",FACE,{"disambiguationData":[TD([[makeQuery(id+"F9.imprint","IMPRINT",EDGE,{"derivedFrom":subQ23}),-1.0]])]});}
            var Q4;
            {var subQ0=sQuery(id+"F9.wireOp",EDGE,"E61.0");var subQ1=sQuery(id+"F9.wireOp",EDGE,"E56.2");var subQ2=makeQuery(id+"F9.imprint","INTERSECT",VERTEX,{"disambiguationData":[OD(1.0)],"derivedFrom":[subQ1,subQ0]});Q4=makeQuery(id+"F9.imprint","IMPRINT",FACE,{"disambiguationData":[TD([[makeQuery(id+"F9.imprint","IMPRINT",EDGE,{"disambiguationData":[TD([[subQ2,-1.0]])],"derivedFrom":subQ1}),-1.0]])]});}
            var Q5;
            {var subQ0=sQuery(id+"F9.wireOp",EDGE,"E56.1");Q5=makeQuery(id+"F9.imprint","IMPRINT",FACE,{"disambiguationData":[TD([[makeQuery(id+"F9.imprint","IMPRINT",EDGE,{"derivedFrom":subQ0}),1.0]])]});}
            var Q6;
            {var subQ0=sQuery(id+"F9.wireOp",EDGE,"E63.0");var subQ1=sQuery(id+"F9.wireOp",EDGE,"E56.0");var subQ2=makeQuery(id+"F9.imprint","INTERSECT",VERTEX,{"disambiguationData":[OD(1.0)],"derivedFrom":[subQ1,subQ0]});Q6=makeQuery(id+"F9.imprint","IMPRINT",FACE,{"disambiguationData":[TD([[makeQuery(id+"F9.imprint","IMPRINT",EDGE,{"disambiguationData":[TD([[subQ2,-1.0]])],"derivedFrom":subQ1}),-1.0]])]});}
            var Q7;
            {var subQ0=sQuery(id+"F0.wireOp",EDGE,"E10.5.0.0");var subQ1=sQuery(id+"F0.wireOp",EDGE,"E10.7.0.0");var subQ2=sQuery(id+"F0.wireOp",EDGE,"E10.6.0.0");var subQ3=sQuery(id+"F0.wireOp",EDGE,"E10.4.0.0");var subQ4=sQuery(id+"F0.wireOp",EDGE,"E10.3.0.0");var subQ5=sQuery(id+"F0.wireOp",EDGE,"E10.2.0.0");var subQ6=sQuery(id+"F0.wireOp",EDGE,"E10.1.0.0");var subQ7=sQuery(id+"F0.wireOp",EDGE,"E9");var subQ8=sQuery(id+"F0.wireOp",EDGE,"E6.MirrorCS");var subQ9=sQuery(id+"F0.wireOp",EDGE,"E5.MirrorCS");var subQ10=sQuery(id+"F0.wireOp",EDGE,"E4.MirrorCS");var subQ11=sQuery(id+"F0.wireOp",EDGE,"E3.MirrorCS");var subQ12=sQuery(id+"F0.wireOp",EDGE,"E1.right");var subQ13=sQuery(id+"F0.wireOp",EDGE,"E1.left");var subQ14=sQuery(id+"F0.wireOp",EDGE,"E1.top");var subQ15=sQuery(id+"F0.wireOp",EDGE,"E1.bottom");Q7=makeQuery(id+"F8.boolean.opBoolean","MERGE",FACE,{"derivedFrom":[makeQuery(id+"F6.boolean.opBoolean","MERGE",FACE,{"derivedFrom":[makeQuery(id+"F4.boolean.opBoolean","MERGE",FACE,{"derivedFrom":[makeQuery(id+"F1.opExtrude","CAP_FACE",FACE,{"disambiguationData":[OSD([subQ15,subQ14,subQ13,subQ12,subQ11,subQ10,subQ9,subQ8,subQ7,subQ6,subQ5,subQ4,subQ3,subQ0,subQ2,subQ1])],"isStart":true}),makeQuery(id+"F4.opExtrude","CAP_FACE",FACE,{"disambiguationData":[OSD([subQ15,subQ14,subQ13,subQ12,subQ11,subQ10,subQ9,subQ8,subQ7,subQ6,subQ5,subQ4,subQ3,subQ0,subQ2,subQ1]),ownerDisambiguation([makeQuery(id+"F4.opExtrude","SWEPT_BODY",BODY,{"disambiguationData":[OSD([sQuery(id+"F3.wireOp",EDGE,"E13"),sQuery(id+"F3.wireOp",EDGE,"E14"),sQuery(id+"F3.wireOp",EDGE,"E15"),sQuery(id+"F3.wireOp",EDGE,"E16"),sQuery(id+"F3.wireOp",EDGE,"E17"),sQuery(id+"F3.wireOp",EDGE,"E18"),sQuery(id+"F3.wireOp",EDGE,"E19"),sQuery(id+"F3.wireOp",EDGE,"E20"),sQuery(id+"F3.wireOp",EDGE,"E21"),sQuery(id+"F3.wireOp",EDGE,"E22.0"),sQuery(id+"F3.wireOp",EDGE,"E23.0"),sQuery(id+"F3.wireOp",EDGE,"E24.0"),sQuery(id+"F3.wireOp",EDGE,"E28")])]})])],"isStart":false}),makeQuery(id+"F4.opExtrude","CAP_FACE",FACE,{"disambiguationData":[OSD([subQ15,subQ14,subQ13,subQ12,subQ11,subQ10,subQ9,subQ8,subQ7,subQ6,subQ5,subQ4,subQ3,subQ0,subQ2,subQ1]),ownerDisambiguation([makeQuery(id+"F4.opExtrude","SWEPT_BODY",BODY,{"disambiguationData":[OSD([sQuery(id+"F3.wireOp",EDGE,"E30.1.2"),sQuery(id+"F3.wireOp",EDGE,"E30.1.3"),sQuery(id+"F3.wireOp",EDGE,"E30.1.4"),sQuery(id+"F3.wireOp",EDGE,"E30.1.5"),sQuery(id+"F3.wireOp",EDGE,"E30.1.6"),sQuery(id+"F3.wireOp",EDGE,"E30.1.7"),sQuery(id+"F3.wireOp",EDGE,"E30.1.8"),sQuery(id+"F3.wireOp",EDGE,"E30.1.9"),sQuery(id+"F3.wireOp",EDGE,"E30.1.10"),sQuery(id+"F3.wireOp",EDGE,"E30.1.11"),sQuery(id+"F3.wireOp",EDGE,"E30.1.12"),sQuery(id+"F3.wireOp",EDGE,"E30.1.13"),sQuery(id+"F3.wireOp",EDGE,"E30.1.14")])]})])],"isStart":false})]}),makeQuery(id+"F6.opExtrude","CAP_FACE",FACE,{"disambiguationData":[OSD([subQ15,subQ14,subQ13,subQ12,subQ11,subQ10,subQ9,subQ8,subQ7,subQ6,subQ5,subQ4,subQ3,subQ0,subQ2,subQ1])],"isStart":false})]}),makeQuery(id+"F8.opExtrude","CAP_FACE",FACE,{"disambiguationData":[OSD([subQ15,subQ14,subQ13,subQ12,subQ11,subQ10,subQ9,subQ8,subQ7,subQ6,subQ5,subQ4,subQ3,subQ0,subQ2,subQ1]),ownerDisambiguation([makeQuery(id+"F8.opExtrude","SWEPT_BODY",BODY,{"disambiguationData":[OSD([subQ0,sQuery(id+"F7.wireOp",EDGE,"E39"),sQuery(id+"F7.wireOp",EDGE,"E40"),sQuery(id+"F7.wireOp",EDGE,"E41"),sQuery(id+"F7.wireOp",EDGE,"E42.0")])]})])],"isStart":false})]});}
            extrude(context, id + "F10", {"entities" : qUnion([Q0, Q1, Q2, Q3, Q4, Q5, Q6]), "operationType" : NewBodyOperationType.ADD, "endBound" : BoundingType.UP_TO_SURFACE, "oppositeDirection" : true, "endBoundEntityFace" : qUnion([Q7]), "depth" : 25.4 * mm});
        }
        {
            var Q0;
            {var subQ0=sQuery(id+"F9.wireOp",EDGE,"E57.7");var subQ1=sQuery(id+"F5.wireOp",EDGE,"E32");var subQ2=sQuery(id+"F5.wireOp",EDGE,"E31");var subQ3=sQuery(id+"F3.wireOp",EDGE,"E15");var subQ4=sQuery(id+"F0.wireOp",EDGE,"E9");var subQ5=sQuery(id+"F9.wireOp",EDGE,"E56.4");var subQ6=sQuery(id+"F0.wireOp",EDGE,"E10.4.0.0");var subQ7=sQuery(id+"F0.wireOp",EDGE,"E10.2.0.0");var subQ8=sQuery(id+"F0.wireOp",EDGE,"E10.7.0.0");var subQ9=sQuery(id+"F0.wireOp",EDGE,"E10.6.0.0");var subQ10=sQuery(id+"F0.wireOp",EDGE,"E10.5.0.0");Q0=makeQuery(id+"F10.boolean.opBoolean","MERGE",FACE,{"derivedFrom":[makeQuery(id+"F8.boolean.opBoolean","MERGE",FACE,{"derivedFrom":[makeQuery(id+"F6.boolean.opBoolean","MERGE",FACE,{"derivedFrom":[makeQuery(id+"F4.boolean.opBoolean","MERGE",FACE,{"derivedFrom":[makeQuery(id+"F1.opExtrude","CAP_FACE",FACE,{"disambiguationData":[OSD([sQuery(id+"F0.wireOp",EDGE,"E1.bottom"),sQuery(id+"F0.wireOp",EDGE,"E1.top"),sQuery(id+"F0.wireOp",EDGE,"E1.left"),sQuery(id+"F0.wireOp",EDGE,"E1.right"),sQuery(id+"F0.wireOp",EDGE,"E3.MirrorCS"),sQuery(id+"F0.wireOp",EDGE,"E4.MirrorCS"),sQuery(id+"F0.wireOp",EDGE,"E5.MirrorCS"),sQuery(id+"F0.wireOp",EDGE,"E6.MirrorCS"),subQ4,sQuery(id+"F0.wireOp",EDGE,"E10.1.0.0"),subQ7,sQuery(id+"F0.wireOp",EDGE,"E10.3.0.0"),subQ6,subQ10,subQ9,subQ8])],"isStart":false}),makeQuery(id+"F4.opExtrude","CAP_FACE",FACE,{"disambiguationData":[OSD([sQuery(id+"F3.wireOp",EDGE,"E13"),sQuery(id+"F3.wireOp",EDGE,"E14"),subQ3,sQuery(id+"F3.wireOp",EDGE,"E16"),sQuery(id+"F3.wireOp",EDGE,"E17"),sQuery(id+"F3.wireOp",EDGE,"E18"),sQuery(id+"F3.wireOp",EDGE,"E19"),sQuery(id+"F3.wireOp",EDGE,"E20"),sQuery(id+"F3.wireOp",EDGE,"E21"),sQuery(id+"F3.wireOp",EDGE,"E22.0"),sQuery(id+"F3.wireOp",EDGE,"E23.0"),sQuery(id+"F3.wireOp",EDGE,"E24.0"),sQuery(id+"F3.wireOp",EDGE,"E28")])],"isStart":true}),makeQuery(id+"F4.opExtrude","CAP_FACE",FACE,{"disambiguationData":[OSD([sQuery(id+"F3.wireOp",EDGE,"E30.1.2"),sQuery(id+"F3.wireOp",EDGE,"E30.1.3"),sQuery(id+"F3.wireOp",EDGE,"E30.1.4"),sQuery(id+"F3.wireOp",EDGE,"E30.1.5"),sQuery(id+"F3.wireOp",EDGE,"E30.1.6"),sQuery(id+"F3.wireOp",EDGE,"E30.1.7"),sQuery(id+"F3.wireOp",EDGE,"E30.1.8"),sQuery(id+"F3.wireOp",EDGE,"E30.1.9"),sQuery(id+"F3.wireOp",EDGE,"E30.1.10"),sQuery(id+"F3.wireOp",EDGE,"E30.1.11"),sQuery(id+"F3.wireOp",EDGE,"E30.1.12"),sQuery(id+"F3.wireOp",EDGE,"E30.1.13"),sQuery(id+"F3.wireOp",EDGE,"E30.1.14")])],"isStart":true})]}),makeQuery(id+"F6.opExtrude","CAP_FACE",FACE,{"disambiguationData":[OSD([subQ2,subQ1,sQuery(id+"F5.wireOp",EDGE,"E33.0"),sQuery(id+"F5.wireOp",EDGE,"E34.0"),sQuery(id+"F5.wireOp",EDGE,"E35.0"),sQuery(id+"F5.wireOp",EDGE,"E36.0")])],"isStart":true})]}),makeQuery(id+"F8.opExtrude","CAP_FACE",FACE,{"disambiguationData":[OSD([subQ10,sQuery(id+"F7.wireOp",EDGE,"E39"),sQuery(id+"F7.wireOp",EDGE,"E40"),sQuery(id+"F7.wireOp",EDGE,"E41"),sQuery(id+"F7.wireOp",EDGE,"E42.0")])],"isStart":true})]}),makeQuery(id+"F10.opExtrude","CAP_FACE",FACE,{"disambiguationData":[OSD([subQ6,subQ9,subQ8,sQuery(id+"F9.wireOp",EDGE,"E56.0"),sQuery(id+"F9.wireOp",EDGE,"E56.1"),sQuery(id+"F9.wireOp",EDGE,"E56.2"),sQuery(id+"F9.wireOp",EDGE,"E56.3"),subQ5,sQuery(id+"F9.wireOp",EDGE,"E57.0"),sQuery(id+"F9.wireOp",EDGE,"E57.1"),sQuery(id+"F9.wireOp",EDGE,"E57.2"),sQuery(id+"F9.wireOp",EDGE,"E57.3"),sQuery(id+"F9.wireOp",EDGE,"E59")])],"isStart":true}),makeQuery(id+"F10.opExtrude","CAP_FACE",FACE,{"disambiguationData":[OSD([subQ7,subQ6,subQ5,sQuery(id+"F9.wireOp",EDGE,"E56.8"),sQuery(id+"F9.wireOp",EDGE,"E57.4"),subQ0,sQuery(id+"F9.wireOp",EDGE,"E57.8")])],"isStart":true}),makeQuery(id+"F10.opExtrude","CAP_FACE",FACE,{"disambiguationData":[OSD([subQ4,subQ3,sQuery(id+"F9.wireOp",EDGE,"E56.5")])],"isStart":true}),makeQuery(id+"F10.opExtrude","CAP_FACE",FACE,{"disambiguationData":[OSD([subQ2,subQ1,sQuery(id+"F9.wireOp",EDGE,"E56.6"),sQuery(id+"F9.wireOp",EDGE,"E56.7"),sQuery(id+"F9.wireOp",EDGE,"E57.5"),sQuery(id+"F9.wireOp",EDGE,"E57.6"),subQ0])],"isStart":true})]});}
            var sketch = newSketch(context, id + "F11", { "sketchPlane" : qUnion([Q0])});
            skLineSegment(sketch, "E64", {"start": v(-163.1, 70.33) * mm, "end": v(-135.66, 37.87) * mm});
            skLineSegment(sketch, "E65", {"start": v(-135.66, 37.87) * mm, "end": v(-140.17, 33.24) * mm});
            skLineSegment(sketch, "E66", {"start": v(-140.17, 33.24) * mm, "end": v(-153.1, 45.84) * mm});
            skLineSegment(sketch, "E67", {"start": v(-153.1, 45.84) * mm, "end": v(-165.14, 35.66) * mm});
            skLineSegment(sketch, "E68", {"start": v(-165.14, 35.66) * mm, "end": v(-183.31, 56.22) * mm});
            skLineSegment(sketch, "E69", {"start": v(-183.31, 56.22) * mm, "end": v(-176.3, 62.42) * mm});
            skLineSegment(sketch, "E70", {"start": v(-176.3, 62.42) * mm, "end": v(-166.09, 47.28) * mm});
            skLineSegment(sketch, "E71", {"start": v(-166.09, 47.28) * mm, "end": v(-159.08, 54.85) * mm});
            skLineSegment(sketch, "E72", {"start": v(-159.08, 54.85) * mm, "end": v(-169.19, 67.3) * mm});
            skLineSegment(sketch, "E73", {"start": v(-169.19, 67.3) * mm, "end": v(-163.1, 70.33) * mm});
            skSolve(sketch);
        }
        {
            var Q0;
            Q0=makeQuery(id+"F11.imprint","IMPRINT",FACE,{"disambiguationData":[TD([[makeQuery(id+"F11.imprint","IMPRINT",EDGE,{"derivedFrom":sQuery(id+"F11.wireOp",EDGE,"E64")}),-1.0]])]});
            extrude(context, id + "F12", {"entities" : qUnion([Q0]), "operationType" : NewBodyOperationType.REMOVE, "endBound" : BoundingType.THROUGH_ALL, "oppositeDirection" : true, "depth" : 25.4 * mm});
        }
        {
            var Q0;
            Q0=makeQuery(id+"F283B0sprifPech_2.boolean.opBoolean","MERGE",FACE,{"derivedFrom":[makeQuery(id+"F1.opExtrude","CAP_FACE",FACE,{"disambiguationData":[OSD([sQuery(id+"F0.wireOp",EDGE,"E1.bottom"),sQuery(id+"F0.wireOp",EDGE,"E1.top"),sQuery(id+"F0.wireOp",EDGE,"E1.left"),sQuery(id+"F0.wireOp",EDGE,"E1.right"),sQuery(id+"F0.wireOp",EDGE,"E4.MirrorCS"),sQuery(id+"F0.wireOp",EDGE,"E5.MirrorCS"),sQuery(id+"F0.wireOp",EDGE,"E6.MirrorCS"),sQuery(id+"F0.wireOp",EDGE,"XP4RUk2x-XywD-8Rss-njOT-CbR3bshOKOK0"),sQuery(id+"F0.wireOp",EDGE,"b9c52205-24cb-4650-8c4e-571e5ae3eca1.0"),sQuery(id+"F0.wireOp",EDGE,"7ce87519-bf1c-46bc-aa78-43c94738a5b50.MirrorCS"),sQuery(id+"F0.wireOp",EDGE,"ccf874e0-e1d4-48cc-add4-a2e5abeee12a0.MirrorCS"),sQuery(id+"F0.wireOp",EDGE,"DQWdHeld-nOTJ-AGL9-kPKw-Er3UUZTjvbz2"),sQuery(id+"F0.wireOp",EDGE,"5bbe5c57-7fd2-4e44-8496-fd152f60ea6d.0"),sQuery(id+"F0.wireOp",EDGE,"2644ac68-4d61-4093-969e-9ed6f096598b0.MirrorCS"),sQuery(id+"F0.wireOp",EDGE,"223ada2f-ac75-4c22-bb8b-c6a36271a7450.MirrorCS")])],"isStart":false}),makeQuery(id+"FbZmjcGa23uXbBk_1.opExtrude","CAP_FACE",FACE,{"disambiguationData":[OSD([sQuery(id+"FDd7BUQnQsR1ERr_1.wireOp",EDGE,"ijLNuKmu-ZImU-8Qy0-qpEc-2hT5XXYOhMIL"),sQuery(id+"FDd7BUQnQsR1ERr_1.wireOp",EDGE,"748e210a-1b09-487e-afb4-84e0041017d20.MirrorCS"),sQuery(id+"FDd7BUQnQsR1ERr_1.wireOp",EDGE,"EbRHtslw-PesK-X2KX-Epd3-5ARW2Y1ADblM"),sQuery(id+"FDd7BUQnQsR1ERr_1.wireOp",EDGE,"36aff3c3-2114-4845-be23-4b4de690cf4e0.MirrorCS")])],"isStart":true}),makeQuery(id+"F283B0sprifPech_2.opExtrude","CAP_FACE",FACE,{"disambiguationData":[OSD([sQuery(id+"FKg46lQX9Lzar0e_2.wireOp",EDGE,"RKsqUNIB-oXuT-FghO-M9Da-QaYfdLgeOogY"),sQuery(id+"FKg46lQX9Lzar0e_2.wireOp",EDGE,"0c2d5422-fc6d-4cf0-94d5-60034e5543d9.0"),sQuery(id+"FKg46lQX9Lzar0e_2.wireOp",EDGE,"ed9859be-94c1-4a58-8602-2c24449e7e3b.0"),sQuery(id+"FKg46lQX9Lzar0e_2.wireOp",EDGE,"fcabd7da-79ea-44d3-b4c3-32c0b349024b.0")])],"isStart":true}),makeQuery(id+"F283B0sprifPech_2.opExtrude","CAP_FACE",FACE,{"disambiguationData":[OSD([sQuery(id+"FKg46lQX9Lzar0e_2.wireOp",EDGE,"PQQcEOAV-w7hQ-vXpY-OJhk-dHFxQkKisjoy"),sQuery(id+"FKg46lQX9Lzar0e_2.wireOp",EDGE,"a2860ae3-f131-4044-94e2-4e286d42ae91.0"),sQuery(id+"FKg46lQX9Lzar0e_2.wireOp",EDGE,"0c9bf0a6-4900-4e51-8f86-4495d1022bcf.0"),sQuery(id+"FKg46lQX9Lzar0e_2.wireOp",EDGE,"0591b98d-f766-4fe3-ab21-a85f29ec3849.0")])],"isStart":true}),makeQuery(id+"F283B0sprifPech_2.opExtrude","CAP_FACE",FACE,{"disambiguationData":[OSD([sQuery(id+"FKg46lQX9Lzar0e_2.wireOp",EDGE,"8fokoyeT-4Fqg-vRdq-gASr-Gts9nVmuAlc1"),sQuery(id+"FKg46lQX9Lzar0e_2.wireOp",EDGE,"e6bf3d82-ae5f-4081-a42c-7b02c2625a03.0"),sQuery(id+"FKg46lQX9Lzar0e_2.wireOp",EDGE,"318bf7e0-d448-403b-b795-23b460f485b7.trimOffspring"),sQuery(id+"FKg46lQX9Lzar0e_2.wireOp",EDGE,"68c10766-09fd-4996-bb26-781cb61321f1.trimOffspring")])],"isStart":true}),makeQuery(id+"F283B0sprifPech_2.opExtrude","CAP_FACE",FACE,{"disambiguationData":[OSD([sQuery(id+"FKg46lQX9Lzar0e_2.wireOp",EDGE,"fNLQk4Zj-YxzV-NaTQ-lUeE-ZAzDsx1Q28cd"),sQuery(id+"FKg46lQX9Lzar0e_2.wireOp",EDGE,"933c0e7e-f390-4ea2-a0ef-15f09eff4502.0"),sQuery(id+"FKg46lQX9Lzar0e_2.wireOp",EDGE,"251da519-fee3-49d7-9020-63256aabe8af.0"),sQuery(id+"FKg46lQX9Lzar0e_2.wireOp",EDGE,"ded70781-7421-4613-802d-a830aa005029.0")])],"isStart":true}),makeQuery(id+"F283B0sprifPech_2.opExtrude","CAP_FACE",FACE,{"disambiguationData":[OSD([sQuery(id+"FKg46lQX9Lzar0e_2.wireOp",EDGE,"h7utIOVY-cyRB-reym-abKA-IaenTZ3oMXoJ"),sQuery(id+"FKg46lQX9Lzar0e_2.wireOp",EDGE,"47fda24c-ec27-4c9a-a8d7-5ffade185e94.0"),sQuery(id+"FKg46lQX9Lzar0e_2.wireOp",EDGE,"027c178f-2cb8-458e-9e04-3a57a83d31e4.0"),sQuery(id+"FKg46lQX9Lzar0e_2.wireOp",EDGE,"d4e33e84-a5d6-41ba-8414-b43a23e185c5.0")])],"isStart":true}),makeQuery(id+"F283B0sprifPech_2.opExtrude","CAP_FACE",FACE,{"disambiguationData":[OSD([sQuery(id+"FKg46lQX9Lzar0e_2.wireOp",EDGE,"r84SJDFy-sy4K-hZXY-K2KP-T5HZfeiNjgwy"),sQuery(id+"FKg46lQX9Lzar0e_2.wireOp",EDGE,"f350c8d4-085c-4ae2-94c8-7a7f816f40c0.0"),sQuery(id+"FKg46lQX9Lzar0e_2.wireOp",EDGE,"d4b299e7-3fb7-4c7e-ac93-65c23b04b865.trimOffspring"),sQuery(id+"FKg46lQX9Lzar0e_2.wireOp",EDGE,"c3567d12-d63a-406a-8048-15a9eb174e73.trimOffspring")])],"isStart":true})]});
            var sketch = newSketch(context, id + "F13", { "sketchPlane" : qUnion([Q0])});
            skLineSegment(sketch, "E74.bottom", {"start": v(462.5, 19.84) * mm, "end": v(425.99, 19.84) * mm});
            skLineSegment(sketch, "E74.top", {"start": v(462.5, -19.84) * mm, "end": v(425.99, -19.84) * mm});
            skLineSegment(sketch, "E74.left", {"start": v(464.09, 18.26) * mm, "end": v(464.09, -18.26) * mm});
            skLineSegment(sketch, "E74.right", {"start": v(424.4, 18.26) * mm, "end": v(424.4, -18.26) * mm});
            skPoint(sketch, "E74.middle", {"position": v(444.25, 0) * mm});
            skLineSegment(sketch, "E75", {"start": v(0, 0) * mm, "end": v(0, 70.37) * mm, "construction": true});
            skPoint(sketch, "E76.visualSharp", {"position": v(424.4, 19.84) * mm});
            skArc(sketch, "E76.filletArc", {"start": v(425.99, 19.84) * mm, "mid": v(424.87, 19.38) * mm, "end": v(424.4, 18.26) * mm});
            skPoint(sketch, "E77.visualSharp", {"position": v(464.09, 19.84) * mm});
            skArc(sketch, "E77.filletArc", {"start": v(464.09, 18.26) * mm, "mid": v(463.62, 19.38) * mm, "end": v(462.5, 19.84) * mm});
            skPoint(sketch, "E78.visualSharp", {"position": v(464.09, -19.84) * mm});
            skArc(sketch, "E78.filletArc", {"start": v(462.5, -19.84) * mm, "mid": v(463.62, -19.38) * mm, "end": v(464.09, -18.26) * mm});
            skPoint(sketch, "E79.visualSharp", {"position": v(424.4, -19.84) * mm});
            skArc(sketch, "E79.filletArc", {"start": v(424.4, -18.26) * mm, "mid": v(424.87, -19.38) * mm, "end": v(425.99, -19.84) * mm});
            skLineSegment(sketch, "E80", {"start": v(438.56, 63.5) * mm, "end": v(444.25, 0) * mm, "construction": true});
            skLineSegment(sketch, "E81", {"start": v(508, 0) * mm, "end": v(444.25, 0) * mm, "construction": true});
            skArc(sketch, "E82.MirrorCS", {"start": v(-462.5, -19.84) * mm, "mid": v(-463.62, -19.38) * mm, "end": v(-464.09, -18.26) * mm});
            skArc(sketch, "E83.MirrorCS", {"start": v(-464.09, 18.26) * mm, "mid": v(-463.62, 19.38) * mm, "end": v(-462.5, 19.84) * mm});
            skArc(sketch, "E84.MirrorCS", {"start": v(-425.99, 19.84) * mm, "mid": v(-424.87, 19.38) * mm, "end": v(-424.4, 18.26) * mm});
            skArc(sketch, "E85.MirrorCS", {"start": v(-424.4, -18.26) * mm, "mid": v(-424.87, -19.38) * mm, "end": v(-425.99, -19.84) * mm});
            skPoint(sketch, "E86.MirrorP", {"position": v(-464.09, -19.84) * mm});
            skLineSegment(sketch, "E87.MirrorCS", {"start": v(-508, 0) * mm, "end": v(-444.25, 0) * mm, "construction": true});
            skLineSegment(sketch, "E88.MirrorCS", {"start": v(-438.56, 63.5) * mm, "end": v(-444.25, 0) * mm, "construction": true});
            skPoint(sketch, "E89.MirrorP", {"position": v(-444.25, 0) * mm});
            skPoint(sketch, "E90.MirrorP", {"position": v(-424.4, -19.84) * mm});
            skLineSegment(sketch, "E91.MirrorCS", {"start": v(-464.09, 18.26) * mm, "end": v(-464.09, -18.26) * mm});
            skLineSegment(sketch, "E92.MirrorCS", {"start": v(-462.5, 19.84) * mm, "end": v(-425.99, 19.84) * mm});
            skPoint(sketch, "E93.MirrorP", {"position": v(-424.4, 19.84) * mm});
            skPoint(sketch, "E94.MirrorP", {"position": v(-464.09, 19.84) * mm});
            skLineSegment(sketch, "E95.MirrorCS", {"start": v(-424.4, 18.26) * mm, "end": v(-424.4, -18.26) * mm});
            skLineSegment(sketch, "E96.MirrorCS", {"start": v(-462.5, -19.84) * mm, "end": v(-425.99, -19.84) * mm});
            skSolve(sketch);
        }
        {
            var Q0;
            Q0=qSketchRegion(id+"F13",true);
            extrude(context, id + "F14", {"entities" : qUnion([Q0]), "operationType" : NewBodyOperationType.REMOVE, "endBound" : BoundingType.THROUGH_ALL, "oppositeDirection" : true, "depth" : 25 * mm});
        }
        {
            var Q0;
            Q0=makeQuery(id+"F283B0sprifPech_2.boolean.opBoolean","MERGE",FACE,{"derivedFrom":[makeQuery(id+"F1.opExtrude","CAP_FACE",FACE,{"disambiguationData":[OSD([sQuery(id+"F0.wireOp",EDGE,"E1.bottom"),sQuery(id+"F0.wireOp",EDGE,"E1.top"),sQuery(id+"F0.wireOp",EDGE,"E1.left"),sQuery(id+"F0.wireOp",EDGE,"E1.right"),sQuery(id+"F0.wireOp",EDGE,"E4.MirrorCS"),sQuery(id+"F0.wireOp",EDGE,"E5.MirrorCS"),sQuery(id+"F0.wireOp",EDGE,"E6.MirrorCS"),sQuery(id+"F0.wireOp",EDGE,"XP4RUk2x-XywD-8Rss-njOT-CbR3bshOKOK0"),sQuery(id+"F0.wireOp",EDGE,"b9c52205-24cb-4650-8c4e-571e5ae3eca1.0"),sQuery(id+"F0.wireOp",EDGE,"7ce87519-bf1c-46bc-aa78-43c94738a5b50.MirrorCS"),sQuery(id+"F0.wireOp",EDGE,"ccf874e0-e1d4-48cc-add4-a2e5abeee12a0.MirrorCS"),sQuery(id+"F0.wireOp",EDGE,"DQWdHeld-nOTJ-AGL9-kPKw-Er3UUZTjvbz2"),sQuery(id+"F0.wireOp",EDGE,"5bbe5c57-7fd2-4e44-8496-fd152f60ea6d.0"),sQuery(id+"F0.wireOp",EDGE,"2644ac68-4d61-4093-969e-9ed6f096598b0.MirrorCS"),sQuery(id+"F0.wireOp",EDGE,"223ada2f-ac75-4c22-bb8b-c6a36271a7450.MirrorCS")])],"isStart":false}),makeQuery(id+"FbZmjcGa23uXbBk_1.opExtrude","CAP_FACE",FACE,{"disambiguationData":[OSD([sQuery(id+"FDd7BUQnQsR1ERr_1.wireOp",EDGE,"ijLNuKmu-ZImU-8Qy0-qpEc-2hT5XXYOhMIL"),sQuery(id+"FDd7BUQnQsR1ERr_1.wireOp",EDGE,"748e210a-1b09-487e-afb4-84e0041017d20.MirrorCS"),sQuery(id+"FDd7BUQnQsR1ERr_1.wireOp",EDGE,"EbRHtslw-PesK-X2KX-Epd3-5ARW2Y1ADblM"),sQuery(id+"FDd7BUQnQsR1ERr_1.wireOp",EDGE,"36aff3c3-2114-4845-be23-4b4de690cf4e0.MirrorCS")])],"isStart":true}),makeQuery(id+"F283B0sprifPech_2.opExtrude","CAP_FACE",FACE,{"disambiguationData":[OSD([sQuery(id+"FKg46lQX9Lzar0e_2.wireOp",EDGE,"RKsqUNIB-oXuT-FghO-M9Da-QaYfdLgeOogY"),sQuery(id+"FKg46lQX9Lzar0e_2.wireOp",EDGE,"0c2d5422-fc6d-4cf0-94d5-60034e5543d9.0"),sQuery(id+"FKg46lQX9Lzar0e_2.wireOp",EDGE,"ed9859be-94c1-4a58-8602-2c24449e7e3b.0"),sQuery(id+"FKg46lQX9Lzar0e_2.wireOp",EDGE,"fcabd7da-79ea-44d3-b4c3-32c0b349024b.0")])],"isStart":true}),makeQuery(id+"F283B0sprifPech_2.opExtrude","CAP_FACE",FACE,{"disambiguationData":[OSD([sQuery(id+"FKg46lQX9Lzar0e_2.wireOp",EDGE,"PQQcEOAV-w7hQ-vXpY-OJhk-dHFxQkKisjoy"),sQuery(id+"FKg46lQX9Lzar0e_2.wireOp",EDGE,"a2860ae3-f131-4044-94e2-4e286d42ae91.0"),sQuery(id+"FKg46lQX9Lzar0e_2.wireOp",EDGE,"0c9bf0a6-4900-4e51-8f86-4495d1022bcf.0"),sQuery(id+"FKg46lQX9Lzar0e_2.wireOp",EDGE,"0591b98d-f766-4fe3-ab21-a85f29ec3849.0")])],"isStart":true}),makeQuery(id+"F283B0sprifPech_2.opExtrude","CAP_FACE",FACE,{"disambiguationData":[OSD([sQuery(id+"FKg46lQX9Lzar0e_2.wireOp",EDGE,"8fokoyeT-4Fqg-vRdq-gASr-Gts9nVmuAlc1"),sQuery(id+"FKg46lQX9Lzar0e_2.wireOp",EDGE,"e6bf3d82-ae5f-4081-a42c-7b02c2625a03.0"),sQuery(id+"FKg46lQX9Lzar0e_2.wireOp",EDGE,"318bf7e0-d448-403b-b795-23b460f485b7.trimOffspring"),sQuery(id+"FKg46lQX9Lzar0e_2.wireOp",EDGE,"68c10766-09fd-4996-bb26-781cb61321f1.trimOffspring")])],"isStart":true}),makeQuery(id+"F283B0sprifPech_2.opExtrude","CAP_FACE",FACE,{"disambiguationData":[OSD([sQuery(id+"FKg46lQX9Lzar0e_2.wireOp",EDGE,"fNLQk4Zj-YxzV-NaTQ-lUeE-ZAzDsx1Q28cd"),sQuery(id+"FKg46lQX9Lzar0e_2.wireOp",EDGE,"933c0e7e-f390-4ea2-a0ef-15f09eff4502.0"),sQuery(id+"FKg46lQX9Lzar0e_2.wireOp",EDGE,"251da519-fee3-49d7-9020-63256aabe8af.0"),sQuery(id+"FKg46lQX9Lzar0e_2.wireOp",EDGE,"ded70781-7421-4613-802d-a830aa005029.0")])],"isStart":true}),makeQuery(id+"F283B0sprifPech_2.opExtrude","CAP_FACE",FACE,{"disambiguationData":[OSD([sQuery(id+"FKg46lQX9Lzar0e_2.wireOp",EDGE,"h7utIOVY-cyRB-reym-abKA-IaenTZ3oMXoJ"),sQuery(id+"FKg46lQX9Lzar0e_2.wireOp",EDGE,"47fda24c-ec27-4c9a-a8d7-5ffade185e94.0"),sQuery(id+"FKg46lQX9Lzar0e_2.wireOp",EDGE,"027c178f-2cb8-458e-9e04-3a57a83d31e4.0"),sQuery(id+"FKg46lQX9Lzar0e_2.wireOp",EDGE,"d4e33e84-a5d6-41ba-8414-b43a23e185c5.0")])],"isStart":true}),makeQuery(id+"F283B0sprifPech_2.opExtrude","CAP_FACE",FACE,{"disambiguationData":[OSD([sQuery(id+"FKg46lQX9Lzar0e_2.wireOp",EDGE,"r84SJDFy-sy4K-hZXY-K2KP-T5HZfeiNjgwy"),sQuery(id+"FKg46lQX9Lzar0e_2.wireOp",EDGE,"f350c8d4-085c-4ae2-94c8-7a7f816f40c0.0"),sQuery(id+"FKg46lQX9Lzar0e_2.wireOp",EDGE,"d4b299e7-3fb7-4c7e-ac93-65c23b04b865.trimOffspring"),sQuery(id+"FKg46lQX9Lzar0e_2.wireOp",EDGE,"c3567d12-d63a-406a-8048-15a9eb174e73.trimOffspring")])],"isStart":true})]});
            var sketch = newSketch(context, id + "F15", { "sketchPlane" : qUnion([Q0])});
            skLineSegment(sketch, "E97", {"start": v(444.25, 19.84) * mm, "end": v(444.25, 0) * mm, "construction": true});
            skPoint(sketch, "E97.endSnap0", {"position": v(464.09, 0) * mm});
            skLineSegment(sketch, "E98", {"start": v(444.25, 0) * mm, "end": v(464.09, 0) * mm, "construction": true});
            skPoint(sketch, "E99", {"position": v(488.7, 44.45) * mm});
            skPoint(sketch, "E100.MirrorP", {"position": v(399.8, 44.45) * mm});
            skPoint(sketch, "E101.MirrorP", {"position": v(488.7, -44.45) * mm});
            skPoint(sketch, "E102.MirrorP", {"position": v(399.8, -44.45) * mm});
            skLineSegment(sketch, "E103", {"start": v(0, 0) * mm, "end": v(0, 40.4) * mm, "construction": true});
            skPoint(sketch, "E104.MirrorP", {"position": v(-399.8, 44.45) * mm});
            skPoint(sketch, "E105.MirrorP", {"position": v(-399.8, -44.45) * mm});
            skPoint(sketch, "E106.MirrorP", {"position": v(-488.7, 44.45) * mm});
            skPoint(sketch, "E107.MirrorP", {"position": v(-488.7, -44.45) * mm});
            skSolve(sketch);
        }
        {
            var Q0;
            Q0=sQuery(id+"F15.wireOp",VERTEX,"E99");
            var Q1;
            Q1=sQuery(id+"F15.wireOp",VERTEX,"E101.MirrorP");
            var Q2;
            Q2=sQuery(id+"F15.wireOp",VERTEX,"E102.MirrorP");
            var Q3;
            Q3=sQuery(id+"F15.wireOp",VERTEX,"E100.MirrorP");
            var Q4;
            Q4=sQuery(id+"F15.wireOp",VERTEX,"E106.MirrorP");
            var Q5;
            Q5=sQuery(id+"F15.wireOp",VERTEX,"E104.MirrorP");
            var Q6;
            Q6=sQuery(id+"F15.wireOp",VERTEX,"E105.MirrorP");
            var Q7;
            Q7=sQuery(id+"F15.wireOp",VERTEX,"E107.MirrorP");
            var Q8;
            Q8=makeQuery(id+"F1.opExtrude","SWEPT_BODY",BODY,{"disambiguationData":[OSD([sQuery(id+"F0.wireOp",EDGE,"E1.bottom"),sQuery(id+"F0.wireOp",EDGE,"E1.top"),sQuery(id+"F0.wireOp",EDGE,"E1.left"),sQuery(id+"F0.wireOp",EDGE,"E1.right"),sQuery(id+"F0.wireOp",EDGE,"E4.MirrorCS"),sQuery(id+"F0.wireOp",EDGE,"E5.MirrorCS"),sQuery(id+"F0.wireOp",EDGE,"E6.MirrorCS"),sQuery(id+"F0.wireOp",EDGE,"XP4RUk2x-XywD-8Rss-njOT-CbR3bshOKOK0"),sQuery(id+"F0.wireOp",EDGE,"b9c52205-24cb-4650-8c4e-571e5ae3eca1.0"),sQuery(id+"F0.wireOp",EDGE,"7ce87519-bf1c-46bc-aa78-43c94738a5b50.MirrorCS"),sQuery(id+"F0.wireOp",EDGE,"ccf874e0-e1d4-48cc-add4-a2e5abeee12a0.MirrorCS"),sQuery(id+"F0.wireOp",EDGE,"DQWdHeld-nOTJ-AGL9-kPKw-Er3UUZTjvbz2"),sQuery(id+"F0.wireOp",EDGE,"5bbe5c57-7fd2-4e44-8496-fd152f60ea6d.0"),sQuery(id+"F0.wireOp",EDGE,"2644ac68-4d61-4093-969e-9ed6f096598b0.MirrorCS"),sQuery(id+"F0.wireOp",EDGE,"223ada2f-ac75-4c22-bb8b-c6a36271a7450.MirrorCS")])]});
            hole(context, id + "F16", {"style" : HoleStyle.SIMPLE, "endStyle" : HoleEndStyle.THROUGH, "standardTappedOrClearance" : lookupTablePath({ "standard" : "ANSI", "fit" : "Normal (ASME)", "size" : "1/4", "type" : "Clearance" }), "standardBlindInLast" : lookupTablePath({ "fit" : "Free", "standard" : "ANSI", "size" : "1/4", "type" : "Clearance" }), "holeDiameter" : 6.76 * mm, "locations" : qUnion([Q0, Q1, Q2, Q3, Q4, Q5, Q6, Q7]), "scope" : qUnion([Q8]), "isTappedThrough" : true});
        }
        {
            var Q0;
            Q0=makeQuery(id+"F283B0sprifPech_2.boolean.opBoolean","MERGE",FACE,{"derivedFrom":[makeQuery(id+"F1.opExtrude","CAP_FACE",FACE,{"disambiguationData":[OSD([sQuery(id+"F0.wireOp",EDGE,"E1.bottom"),sQuery(id+"F0.wireOp",EDGE,"E1.top"),sQuery(id+"F0.wireOp",EDGE,"E1.left"),sQuery(id+"F0.wireOp",EDGE,"E1.right"),sQuery(id+"F0.wireOp",EDGE,"E4.MirrorCS"),sQuery(id+"F0.wireOp",EDGE,"E5.MirrorCS"),sQuery(id+"F0.wireOp",EDGE,"E6.MirrorCS"),sQuery(id+"F0.wireOp",EDGE,"XP4RUk2x-XywD-8Rss-njOT-CbR3bshOKOK0"),sQuery(id+"F0.wireOp",EDGE,"b9c52205-24cb-4650-8c4e-571e5ae3eca1.0"),sQuery(id+"F0.wireOp",EDGE,"7ce87519-bf1c-46bc-aa78-43c94738a5b50.MirrorCS"),sQuery(id+"F0.wireOp",EDGE,"ccf874e0-e1d4-48cc-add4-a2e5abeee12a0.MirrorCS"),sQuery(id+"F0.wireOp",EDGE,"DQWdHeld-nOTJ-AGL9-kPKw-Er3UUZTjvbz2"),sQuery(id+"F0.wireOp",EDGE,"5bbe5c57-7fd2-4e44-8496-fd152f60ea6d.0"),sQuery(id+"F0.wireOp",EDGE,"2644ac68-4d61-4093-969e-9ed6f096598b0.MirrorCS"),sQuery(id+"F0.wireOp",EDGE,"223ada2f-ac75-4c22-bb8b-c6a36271a7450.MirrorCS")])],"isStart":false}),makeQuery(id+"FbZmjcGa23uXbBk_1.opExtrude","CAP_FACE",FACE,{"disambiguationData":[OSD([sQuery(id+"FDd7BUQnQsR1ERr_1.wireOp",EDGE,"ijLNuKmu-ZImU-8Qy0-qpEc-2hT5XXYOhMIL"),sQuery(id+"FDd7BUQnQsR1ERr_1.wireOp",EDGE,"748e210a-1b09-487e-afb4-84e0041017d20.MirrorCS"),sQuery(id+"FDd7BUQnQsR1ERr_1.wireOp",EDGE,"EbRHtslw-PesK-X2KX-Epd3-5ARW2Y1ADblM"),sQuery(id+"FDd7BUQnQsR1ERr_1.wireOp",EDGE,"36aff3c3-2114-4845-be23-4b4de690cf4e0.MirrorCS")])],"isStart":true}),makeQuery(id+"F283B0sprifPech_2.opExtrude","CAP_FACE",FACE,{"disambiguationData":[OSD([sQuery(id+"FKg46lQX9Lzar0e_2.wireOp",EDGE,"RKsqUNIB-oXuT-FghO-M9Da-QaYfdLgeOogY"),sQuery(id+"FKg46lQX9Lzar0e_2.wireOp",EDGE,"0c2d5422-fc6d-4cf0-94d5-60034e5543d9.0"),sQuery(id+"FKg46lQX9Lzar0e_2.wireOp",EDGE,"ed9859be-94c1-4a58-8602-2c24449e7e3b.0"),sQuery(id+"FKg46lQX9Lzar0e_2.wireOp",EDGE,"fcabd7da-79ea-44d3-b4c3-32c0b349024b.0")])],"isStart":true}),makeQuery(id+"F283B0sprifPech_2.opExtrude","CAP_FACE",FACE,{"disambiguationData":[OSD([sQuery(id+"FKg46lQX9Lzar0e_2.wireOp",EDGE,"PQQcEOAV-w7hQ-vXpY-OJhk-dHFxQkKisjoy"),sQuery(id+"FKg46lQX9Lzar0e_2.wireOp",EDGE,"a2860ae3-f131-4044-94e2-4e286d42ae91.0"),sQuery(id+"FKg46lQX9Lzar0e_2.wireOp",EDGE,"0c9bf0a6-4900-4e51-8f86-4495d1022bcf.0"),sQuery(id+"FKg46lQX9Lzar0e_2.wireOp",EDGE,"0591b98d-f766-4fe3-ab21-a85f29ec3849.0")])],"isStart":true}),makeQuery(id+"F283B0sprifPech_2.opExtrude","CAP_FACE",FACE,{"disambiguationData":[OSD([sQuery(id+"FKg46lQX9Lzar0e_2.wireOp",EDGE,"8fokoyeT-4Fqg-vRdq-gASr-Gts9nVmuAlc1"),sQuery(id+"FKg46lQX9Lzar0e_2.wireOp",EDGE,"e6bf3d82-ae5f-4081-a42c-7b02c2625a03.0"),sQuery(id+"FKg46lQX9Lzar0e_2.wireOp",EDGE,"318bf7e0-d448-403b-b795-23b460f485b7.trimOffspring"),sQuery(id+"FKg46lQX9Lzar0e_2.wireOp",EDGE,"68c10766-09fd-4996-bb26-781cb61321f1.trimOffspring")])],"isStart":true}),makeQuery(id+"F283B0sprifPech_2.opExtrude","CAP_FACE",FACE,{"disambiguationData":[OSD([sQuery(id+"FKg46lQX9Lzar0e_2.wireOp",EDGE,"fNLQk4Zj-YxzV-NaTQ-lUeE-ZAzDsx1Q28cd"),sQuery(id+"FKg46lQX9Lzar0e_2.wireOp",EDGE,"933c0e7e-f390-4ea2-a0ef-15f09eff4502.0"),sQuery(id+"FKg46lQX9Lzar0e_2.wireOp",EDGE,"251da519-fee3-49d7-9020-63256aabe8af.0"),sQuery(id+"FKg46lQX9Lzar0e_2.wireOp",EDGE,"ded70781-7421-4613-802d-a830aa005029.0")])],"isStart":true}),makeQuery(id+"F283B0sprifPech_2.opExtrude","CAP_FACE",FACE,{"disambiguationData":[OSD([sQuery(id+"FKg46lQX9Lzar0e_2.wireOp",EDGE,"h7utIOVY-cyRB-reym-abKA-IaenTZ3oMXoJ"),sQuery(id+"FKg46lQX9Lzar0e_2.wireOp",EDGE,"47fda24c-ec27-4c9a-a8d7-5ffade185e94.0"),sQuery(id+"FKg46lQX9Lzar0e_2.wireOp",EDGE,"027c178f-2cb8-458e-9e04-3a57a83d31e4.0"),sQuery(id+"FKg46lQX9Lzar0e_2.wireOp",EDGE,"d4e33e84-a5d6-41ba-8414-b43a23e185c5.0")])],"isStart":true}),makeQuery(id+"F283B0sprifPech_2.opExtrude","CAP_FACE",FACE,{"disambiguationData":[OSD([sQuery(id+"FKg46lQX9Lzar0e_2.wireOp",EDGE,"r84SJDFy-sy4K-hZXY-K2KP-T5HZfeiNjgwy"),sQuery(id+"FKg46lQX9Lzar0e_2.wireOp",EDGE,"f350c8d4-085c-4ae2-94c8-7a7f816f40c0.0"),sQuery(id+"FKg46lQX9Lzar0e_2.wireOp",EDGE,"d4b299e7-3fb7-4c7e-ac93-65c23b04b865.trimOffspring"),sQuery(id+"FKg46lQX9Lzar0e_2.wireOp",EDGE,"c3567d12-d63a-406a-8048-15a9eb174e73.trimOffspring")])],"isStart":true})]});
            var sketch = newSketch(context, id + "F17", { "sketchPlane" : qUnion([Q0])});
            skLineSegment(sketch, "E108", {"start": v(0, 0) * mm, "end": v(57.05, 0) * mm, "construction": true});
            skPoint(sketch, "E109", {"position": v(-336.55, 0) * mm});
            skPoint(sketch, "E110", {"position": v(-240.4, 0) * mm});
            skPoint(sketch, "E111", {"position": v(-48.08, 0) * mm});
            skPoint(sketch, "E112", {"position": v(144.24, 0) * mm});
            skPoint(sketch, "E113", {"position": v(240.4, 0) * mm});
            skPoint(sketch, "E114", {"position": v(48.08, 0) * mm});
            skPoint(sketch, "E115", {"position": v(336.55, 0) * mm});
            skLineSegment(sketch, "E116", {"start": v(0, 0) * mm, "end": v(0, 60.1) * mm, "construction": true});
            skPoint(sketch, "E117.MirrorP", {"position": v(-144.24, 0) * mm});
            skPoint(sketch, "E118", {"position": v(382.03, -43.74) * mm});
            skSolve(sketch);
        }
        {
            var Q0;
            Q0=sQuery(id+"F17.wireOp",VERTEX,"E109");
            var Q1;
            Q1=sQuery(id+"F17.wireOp",VERTEX,"E110");
            var Q2;
            Q2=sQuery(id+"F17.wireOp",VERTEX,"E111");
            var Q3;
            Q3=sQuery(id+"F17.wireOp",VERTEX,"E112");
            var Q4;
            Q4=sQuery(id+"F17.wireOp",VERTEX,"E113");
            var Q5;
            Q5=sQuery(id+"F17.wireOp",VERTEX,"E114");
            var Q6;
            Q6=sQuery(id+"F17.wireOp",VERTEX,"bb0bc0e7-1bda-4cdf-bacd-3a9d4629f258");
            var Q7;
            Q7=sQuery(id+"F17.wireOp",VERTEX,"E115");
            var Q8;
            Q8=sQuery(id+"F17.wireOp",VERTEX,"E117.MirrorP");
            var Q9;
            Q9=makeQuery(id+"F1.opExtrude","SWEPT_BODY",BODY,{"disambiguationData":[OSD([sQuery(id+"F0.wireOp",EDGE,"E1.bottom"),sQuery(id+"F0.wireOp",EDGE,"E1.top"),sQuery(id+"F0.wireOp",EDGE,"E1.left"),sQuery(id+"F0.wireOp",EDGE,"E1.right"),sQuery(id+"F0.wireOp",EDGE,"E4.MirrorCS"),sQuery(id+"F0.wireOp",EDGE,"E5.MirrorCS"),sQuery(id+"F0.wireOp",EDGE,"E6.MirrorCS"),sQuery(id+"F0.wireOp",EDGE,"XP4RUk2x-XywD-8Rss-njOT-CbR3bshOKOK0"),sQuery(id+"F0.wireOp",EDGE,"b9c52205-24cb-4650-8c4e-571e5ae3eca1.0"),sQuery(id+"F0.wireOp",EDGE,"7ce87519-bf1c-46bc-aa78-43c94738a5b50.MirrorCS"),sQuery(id+"F0.wireOp",EDGE,"ccf874e0-e1d4-48cc-add4-a2e5abeee12a0.MirrorCS"),sQuery(id+"F0.wireOp",EDGE,"DQWdHeld-nOTJ-AGL9-kPKw-Er3UUZTjvbz2"),sQuery(id+"F0.wireOp",EDGE,"5bbe5c57-7fd2-4e44-8496-fd152f60ea6d.0"),sQuery(id+"F0.wireOp",EDGE,"2644ac68-4d61-4093-969e-9ed6f096598b0.MirrorCS"),sQuery(id+"F0.wireOp",EDGE,"223ada2f-ac75-4c22-bb8b-c6a36271a7450.MirrorCS")])]});
            hole(context, id + "F18", {"style" : HoleStyle.SIMPLE, "endStyle" : HoleEndStyle.THROUGH, "holeDiameter" : 31.75 * mm, "locations" : qUnion([Q0, Q1, Q2, Q3, Q4, Q5, Q6, Q7, Q8]), "scope" : qUnion([Q9]), "isTappedThrough" : true});
        }
        {
            var Q0;
            Q0=makeQuery(id+"F283B0sprifPech_2.boolean.opBoolean","MERGE",FACE,{"derivedFrom":[makeQuery(id+"F1.opExtrude","CAP_FACE",FACE,{"disambiguationData":[OSD([sQuery(id+"F0.wireOp",EDGE,"E1.bottom"),sQuery(id+"F0.wireOp",EDGE,"E1.top"),sQuery(id+"F0.wireOp",EDGE,"E1.left"),sQuery(id+"F0.wireOp",EDGE,"E1.right"),sQuery(id+"F0.wireOp",EDGE,"E4.MirrorCS"),sQuery(id+"F0.wireOp",EDGE,"E5.MirrorCS"),sQuery(id+"F0.wireOp",EDGE,"E6.MirrorCS"),sQuery(id+"F0.wireOp",EDGE,"XP4RUk2x-XywD-8Rss-njOT-CbR3bshOKOK0"),sQuery(id+"F0.wireOp",EDGE,"b9c52205-24cb-4650-8c4e-571e5ae3eca1.0"),sQuery(id+"F0.wireOp",EDGE,"7ce87519-bf1c-46bc-aa78-43c94738a5b50.MirrorCS"),sQuery(id+"F0.wireOp",EDGE,"ccf874e0-e1d4-48cc-add4-a2e5abeee12a0.MirrorCS"),sQuery(id+"F0.wireOp",EDGE,"DQWdHeld-nOTJ-AGL9-kPKw-Er3UUZTjvbz2"),sQuery(id+"F0.wireOp",EDGE,"5bbe5c57-7fd2-4e44-8496-fd152f60ea6d.0"),sQuery(id+"F0.wireOp",EDGE,"2644ac68-4d61-4093-969e-9ed6f096598b0.MirrorCS"),sQuery(id+"F0.wireOp",EDGE,"223ada2f-ac75-4c22-bb8b-c6a36271a7450.MirrorCS")])],"isStart":false}),makeQuery(id+"FbZmjcGa23uXbBk_1.opExtrude","CAP_FACE",FACE,{"disambiguationData":[OSD([sQuery(id+"FDd7BUQnQsR1ERr_1.wireOp",EDGE,"ijLNuKmu-ZImU-8Qy0-qpEc-2hT5XXYOhMIL"),sQuery(id+"FDd7BUQnQsR1ERr_1.wireOp",EDGE,"748e210a-1b09-487e-afb4-84e0041017d20.MirrorCS"),sQuery(id+"FDd7BUQnQsR1ERr_1.wireOp",EDGE,"EbRHtslw-PesK-X2KX-Epd3-5ARW2Y1ADblM"),sQuery(id+"FDd7BUQnQsR1ERr_1.wireOp",EDGE,"36aff3c3-2114-4845-be23-4b4de690cf4e0.MirrorCS")])],"isStart":true}),makeQuery(id+"F283B0sprifPech_2.opExtrude","CAP_FACE",FACE,{"disambiguationData":[OSD([sQuery(id+"FKg46lQX9Lzar0e_2.wireOp",EDGE,"RKsqUNIB-oXuT-FghO-M9Da-QaYfdLgeOogY"),sQuery(id+"FKg46lQX9Lzar0e_2.wireOp",EDGE,"0c2d5422-fc6d-4cf0-94d5-60034e5543d9.0"),sQuery(id+"FKg46lQX9Lzar0e_2.wireOp",EDGE,"ed9859be-94c1-4a58-8602-2c24449e7e3b.0"),sQuery(id+"FKg46lQX9Lzar0e_2.wireOp",EDGE,"fcabd7da-79ea-44d3-b4c3-32c0b349024b.0")])],"isStart":true}),makeQuery(id+"F283B0sprifPech_2.opExtrude","CAP_FACE",FACE,{"disambiguationData":[OSD([sQuery(id+"FKg46lQX9Lzar0e_2.wireOp",EDGE,"PQQcEOAV-w7hQ-vXpY-OJhk-dHFxQkKisjoy"),sQuery(id+"FKg46lQX9Lzar0e_2.wireOp",EDGE,"a2860ae3-f131-4044-94e2-4e286d42ae91.0"),sQuery(id+"FKg46lQX9Lzar0e_2.wireOp",EDGE,"0c9bf0a6-4900-4e51-8f86-4495d1022bcf.0"),sQuery(id+"FKg46lQX9Lzar0e_2.wireOp",EDGE,"0591b98d-f766-4fe3-ab21-a85f29ec3849.0")])],"isStart":true}),makeQuery(id+"F283B0sprifPech_2.opExtrude","CAP_FACE",FACE,{"disambiguationData":[OSD([sQuery(id+"FKg46lQX9Lzar0e_2.wireOp",EDGE,"8fokoyeT-4Fqg-vRdq-gASr-Gts9nVmuAlc1"),sQuery(id+"FKg46lQX9Lzar0e_2.wireOp",EDGE,"e6bf3d82-ae5f-4081-a42c-7b02c2625a03.0"),sQuery(id+"FKg46lQX9Lzar0e_2.wireOp",EDGE,"318bf7e0-d448-403b-b795-23b460f485b7.trimOffspring"),sQuery(id+"FKg46lQX9Lzar0e_2.wireOp",EDGE,"68c10766-09fd-4996-bb26-781cb61321f1.trimOffspring")])],"isStart":true}),makeQuery(id+"F283B0sprifPech_2.opExtrude","CAP_FACE",FACE,{"disambiguationData":[OSD([sQuery(id+"FKg46lQX9Lzar0e_2.wireOp",EDGE,"fNLQk4Zj-YxzV-NaTQ-lUeE-ZAzDsx1Q28cd"),sQuery(id+"FKg46lQX9Lzar0e_2.wireOp",EDGE,"933c0e7e-f390-4ea2-a0ef-15f09eff4502.0"),sQuery(id+"FKg46lQX9Lzar0e_2.wireOp",EDGE,"251da519-fee3-49d7-9020-63256aabe8af.0"),sQuery(id+"FKg46lQX9Lzar0e_2.wireOp",EDGE,"ded70781-7421-4613-802d-a830aa005029.0")])],"isStart":true}),makeQuery(id+"F283B0sprifPech_2.opExtrude","CAP_FACE",FACE,{"disambiguationData":[OSD([sQuery(id+"FKg46lQX9Lzar0e_2.wireOp",EDGE,"h7utIOVY-cyRB-reym-abKA-IaenTZ3oMXoJ"),sQuery(id+"FKg46lQX9Lzar0e_2.wireOp",EDGE,"47fda24c-ec27-4c9a-a8d7-5ffade185e94.0"),sQuery(id+"FKg46lQX9Lzar0e_2.wireOp",EDGE,"027c178f-2cb8-458e-9e04-3a57a83d31e4.0"),sQuery(id+"FKg46lQX9Lzar0e_2.wireOp",EDGE,"d4e33e84-a5d6-41ba-8414-b43a23e185c5.0")])],"isStart":true}),makeQuery(id+"F283B0sprifPech_2.opExtrude","CAP_FACE",FACE,{"disambiguationData":[OSD([sQuery(id+"FKg46lQX9Lzar0e_2.wireOp",EDGE,"r84SJDFy-sy4K-hZXY-K2KP-T5HZfeiNjgwy"),sQuery(id+"FKg46lQX9Lzar0e_2.wireOp",EDGE,"f350c8d4-085c-4ae2-94c8-7a7f816f40c0.0"),sQuery(id+"FKg46lQX9Lzar0e_2.wireOp",EDGE,"d4b299e7-3fb7-4c7e-ac93-65c23b04b865.trimOffspring"),sQuery(id+"FKg46lQX9Lzar0e_2.wireOp",EDGE,"c3567d12-d63a-406a-8048-15a9eb174e73.trimOffspring")])],"isStart":true})]});
            var sketch = newSketch(context, id + "F19", { "sketchPlane" : qUnion([Q0])});
            skLineSegment(sketch, "E119", {"start": v(-336.55, 0) * mm, "end": v(-336.55, -33.85) * mm, "construction": true});
            skPoint(sketch, "E120", {"position": v(-311.15, 0) * mm});
            skPoint(sketch, "E121.MirrorP", {"position": v(-361.95, 0) * mm});
            skLineSegment(sketch, "E122", {"start": v(-311.15, 0) * mm, "end": v(-361.95, 0) * mm, "construction": true});
            skLineSegment(sketch, "E123", {"start": v(-265.8, 0) * mm, "end": v(-215, 0) * mm});
            skLineSegment(sketch, "E124", {"start": v(-73.48, 0) * mm, "end": v(-22.68, 0) * mm});
            skLineSegment(sketch, "E125", {"start": v(118.84, 0) * mm, "end": v(169.64, 0) * mm});
            skLineSegment(sketch, "E126", {"start": v(265.8, 0) * mm, "end": v(215, 0) * mm});
            skLineSegment(sketch, "E127", {"start": v(73.48, 0) * mm, "end": v(22.68, 0) * mm});
            skLineSegment(sketch, "E128", {"start": v(-118.84, 0) * mm, "end": v(-169.64, 0) * mm});
            skLineSegment(sketch, "E129", {"start": v(361.95, 0) * mm, "end": v(311.15, 0) * mm});
            skSolve(sketch);
        }
        {
            var Q0;
            Q0=sQuery(id+"F19.wireOp",VERTEX,"E122.end");
            var Q1;
            Q1=sQuery(id+"F19.wireOp",VERTEX,"E123.start");
            var Q2;
            Q2=sQuery(id+"F19.wireOp",VERTEX,"E123.end");
            var Q3;
            Q3=sQuery(id+"F19.wireOp",VERTEX,"E128.end");
            var Q4;
            Q4=sQuery(id+"F19.wireOp",VERTEX,"E128.start");
            var Q5;
            Q5=sQuery(id+"F19.wireOp",VERTEX,"E124.start");
            var Q6;
            Q6=sQuery(id+"F19.wireOp",VERTEX,"E124.end");
            var Q7;
            Q7=sQuery(id+"F19.wireOp",VERTEX,"E127.end");
            var Q8;
            Q8=sQuery(id+"F19.wireOp",VERTEX,"E127.start");
            var Q9;
            Q9=sQuery(id+"F19.wireOp",VERTEX,"E125.start");
            var Q10;
            Q10=sQuery(id+"F19.wireOp",VERTEX,"E125.end");
            var Q11;
            Q11=sQuery(id+"F19.wireOp",VERTEX,"E126.start");
            var Q12;
            Q12=sQuery(id+"F19.wireOp",VERTEX,"E129.end");
            var Q13;
            Q13=sQuery(id+"F19.wireOp",VERTEX,"E129.start");
            var Q14;
            Q14=sQuery(id+"F19.wireOp",VERTEX,"E120");
            var Q15;
            Q15=makeQuery(id+"F1.opExtrude","SWEPT_BODY",BODY,{"disambiguationData":[OSD([sQuery(id+"F0.wireOp",EDGE,"E1.bottom"),sQuery(id+"F0.wireOp",EDGE,"E1.top"),sQuery(id+"F0.wireOp",EDGE,"E1.left"),sQuery(id+"F0.wireOp",EDGE,"E1.right"),sQuery(id+"F0.wireOp",EDGE,"E3.MirrorCS"),sQuery(id+"F0.wireOp",EDGE,"E4.MirrorCS"),sQuery(id+"F0.wireOp",EDGE,"E5.MirrorCS"),sQuery(id+"F0.wireOp",EDGE,"E6.MirrorCS"),sQuery(id+"F0.wireOp",EDGE,"E9"),sQuery(id+"F0.wireOp",EDGE,"E10.1.0.0"),sQuery(id+"F0.wireOp",EDGE,"E10.2.0.0"),sQuery(id+"F0.wireOp",EDGE,"E10.3.0.0"),sQuery(id+"F0.wireOp",EDGE,"E10.4.0.0"),sQuery(id+"F0.wireOp",EDGE,"E10.5.0.0"),sQuery(id+"F0.wireOp",EDGE,"E10.6.0.0"),sQuery(id+"F0.wireOp",EDGE,"E10.7.0.0")])]});
            hole(context, id + "F20", {"style" : HoleStyle.SIMPLE, "endStyle" : HoleEndStyle.THROUGH, "holeDiameter" : 4.76 * mm, "locations" : qUnion([Q0, Q1, Q2, Q3, Q4, Q5, Q6, Q7, Q8, Q9, Q10, Q11, Q12, Q13, Q14]), "scope" : qUnion([Q15]), "isTappedThrough" : true});
        }
        {
            var Q0;
            {var subQ0=sQuery(id+"F0.wireOp",EDGE,"E9");var subQ1=sQuery(id+"F0.wireOp",EDGE,"E3.MirrorCS");Q0=makeQuery(id+"F1.opExtrude","SWEPT_EDGE",EDGE,{"disambiguationData":[OSD([subQ1,subQ0]),TDD([makeQuery(id+"F0.imprint","INTERSECT",VERTEX,{"disambiguationData":[OD(1.0)],"derivedFrom":[subQ1,subQ0]})])]});}
            var Q1;
            Q1=makeQuery(id+"F4.opExtrude","SWEPT_EDGE",EDGE,{"disambiguationData":[OSD([sQuery(id+"F3.wireOp",EDGE,"E18"),sQuery(id+"F3.wireOp",EDGE,"E19")])]});
            var Q2;
            Q2=makeQuery(id+"F4.opExtrude","SWEPT_EDGE",EDGE,{"disambiguationData":[OSD([sQuery(id+"F3.wireOp",EDGE,"E17"),sQuery(id+"F3.wireOp",EDGE,"E18")])]});
            var Q3;
            Q3=makeQuery(id+"F4.opExtrude","SWEPT_EDGE",EDGE,{"disambiguationData":[OSD([sQuery(id+"F3.wireOp",EDGE,"E16"),sQuery(id+"F3.wireOp",EDGE,"E17")])]});
            var Q4;
            Q4=makeQuery(id+"F4.opExtrude","SWEPT_EDGE",EDGE,{"disambiguationData":[OSD([sQuery(id+"F3.wireOp",EDGE,"E15"),sQuery(id+"F3.wireOp",EDGE,"E16")])]});
            var Q5;
            Q5=makeQuery(id+"F10.opExtrude","SWEPT_EDGE",EDGE,{"disambiguationData":[OSD([sQuery(id+"F3.wireOp",EDGE,"E15"),sQuery(id+"F9.wireOp",EDGE,"E56.5")])]});
            var Q6;
            Q6=makeQuery(id+"F4.opExtrude","SWEPT_EDGE",EDGE,{"disambiguationData":[OSD([sQuery(id+"F3.wireOp",EDGE,"E13"),sQuery(id+"F3.wireOp",EDGE,"E14")])]});
            var Q7;
            Q7=makeQuery(id+"F4.boolean.opBoolean","INTERSECT",EDGE,{"derivedFrom":[makeQuery(id+"F1.opExtrude","SWEPT_FACE",FACE,{"disambiguationData":[OSD([sQuery(id+"F0.wireOp",EDGE,"E5.MirrorCS")])]}),makeQuery(id+"F4.opExtrude","SWEPT_FACE",FACE,{"disambiguationData":[OSD([sQuery(id+"F3.wireOp",EDGE,"E28")])]})]});
            var Q8;
            Q8=makeQuery(id+"F4.opExtrude","SWEPT_EDGE",EDGE,{"disambiguationData":[OSD([sQuery(id+"F3.wireOp",EDGE,"E21"),sQuery(id+"F3.wireOp",EDGE,"E28")])]});
            var Q9;
            {var subQ0=sQuery(id+"F0.wireOp",EDGE,"E9");var subQ1=sQuery(id+"F0.wireOp",EDGE,"E3.MirrorCS");Q9=makeQuery(id+"F1.opExtrude","SWEPT_EDGE",EDGE,{"disambiguationData":[OSD([subQ1,subQ0]),TDD([makeQuery(id+"F0.imprint","INTERSECT",VERTEX,{"disambiguationData":[OD(0.0)],"derivedFrom":[subQ1,subQ0]})])]});}
            var Q10;
            Q10=makeQuery(id+"F6.opExtrude","SWEPT_EDGE",EDGE,{"disambiguationData":[OSD([sQuery(id+"F0.wireOp",EDGE,"E9"),sQuery(id+"F5.wireOp",EDGE,"E32"),sQuery(id+"F5.wireOp",EDGE,"E36.0")])]});
            var Q11;
            {var subQ0=sQuery(id+"F0.wireOp",EDGE,"E10.1.0.0");var subQ1=sQuery(id+"F0.wireOp",EDGE,"E9");Q11=makeQuery(id+"F1.opExtrude","SWEPT_EDGE",EDGE,{"disambiguationData":[OSD([subQ1,subQ0]),TDD([makeQuery(id+"F0.imprint","INTERSECT",VERTEX,{"disambiguationData":[OD(1.0)],"derivedFrom":[subQ1,subQ0]})])]});}
            var Q12;
            {var subQ0=sQuery(id+"F0.wireOp",EDGE,"E10.2.0.0");var subQ1=sQuery(id+"F0.wireOp",EDGE,"E10.1.0.0");Q12=makeQuery(id+"F1.opExtrude","SWEPT_EDGE",EDGE,{"disambiguationData":[OSD([subQ1,subQ0]),TDD([makeQuery(id+"F0.imprint","INTERSECT",VERTEX,{"disambiguationData":[OD(1.0)],"derivedFrom":[subQ1,subQ0]})])]});}
            var Q13;
            Q13=makeQuery(id+"F10.opExtrude","SWEPT_EDGE",EDGE,{"disambiguationData":[OSD([sQuery(id+"F0.wireOp",EDGE,"E10.2.0.0"),sQuery(id+"F9.wireOp",EDGE,"E56.8")])]});
            var Q14;
            Q14=makeQuery(id+"F10.opExtrude","SWEPT_EDGE",EDGE,{"disambiguationData":[OSD([sQuery(id+"F0.wireOp",EDGE,"E10.2.0.0"),sQuery(id+"F9.wireOp",EDGE,"E57.7")])]});
            var Q15;
            {var subQ0=sQuery(id+"F0.wireOp",EDGE,"E10.3.0.0");var subQ1=sQuery(id+"F0.wireOp",EDGE,"E10.2.0.0");Q15=makeQuery(id+"F1.opExtrude","SWEPT_EDGE",EDGE,{"disambiguationData":[OSD([subQ1,subQ0]),TDD([makeQuery(id+"F0.imprint","INTERSECT",VERTEX,{"disambiguationData":[OD(1.0)],"derivedFrom":[subQ1,subQ0]})])]});}
            var Q16;
            {var subQ0=sQuery(id+"F0.wireOp",EDGE,"E10.4.0.0");var subQ1=sQuery(id+"F0.wireOp",EDGE,"E10.3.0.0");Q16=makeQuery(id+"F1.opExtrude","SWEPT_EDGE",EDGE,{"disambiguationData":[OSD([subQ1,subQ0]),TDD([makeQuery(id+"F0.imprint","INTERSECT",VERTEX,{"disambiguationData":[OD(1.0)],"derivedFrom":[subQ1,subQ0]})])]});}
            var Q17;
            Q17=makeQuery(id+"F10.opExtrude","SWEPT_EDGE",EDGE,{"disambiguationData":[OSD([sQuery(id+"F0.wireOp",EDGE,"E10.4.0.0"),sQuery(id+"F9.wireOp",EDGE,"E57.4")])]});
            var Q18;
            {var subQ0=sQuery(id+"F0.wireOp",EDGE,"E10.5.0.0");var subQ1=sQuery(id+"F0.wireOp",EDGE,"E10.4.0.0");Q18=makeQuery(id+"F1.opExtrude","SWEPT_EDGE",EDGE,{"disambiguationData":[OSD([subQ1,subQ0]),TDD([makeQuery(id+"F0.imprint","INTERSECT",VERTEX,{"disambiguationData":[OD(1.0)],"derivedFrom":[subQ1,subQ0]})])]});}
            var Q19;
            Q19=makeQuery(id+"F8.opExtrude","SWEPT_EDGE",EDGE,{"disambiguationData":[OSD([sQuery(id+"F0.wireOp",EDGE,"E10.5.0.0"),sQuery(id+"F7.wireOp",EDGE,"E40")])]});
            var Q20;
            Q20=makeQuery(id+"F8.opExtrude","SWEPT_EDGE",EDGE,{"disambiguationData":[OSD([sQuery(id+"F7.wireOp",EDGE,"E39"),sQuery(id+"F7.wireOp",EDGE,"E40")])]});
            var Q21;
            Q21=makeQuery(id+"F8.opExtrude","SWEPT_EDGE",EDGE,{"disambiguationData":[OSD([sQuery(id+"F0.wireOp",EDGE,"E10.5.0.0"),sQuery(id+"F7.wireOp",EDGE,"E41")])]});
            var Q22;
            {var subQ0=sQuery(id+"F0.wireOp",EDGE,"E10.6.0.0");var subQ1=sQuery(id+"F0.wireOp",EDGE,"E10.5.0.0");Q22=makeQuery(id+"F1.opExtrude","SWEPT_EDGE",EDGE,{"disambiguationData":[OSD([subQ1,subQ0]),TDD([makeQuery(id+"F0.imprint","INTERSECT",VERTEX,{"disambiguationData":[OD(1.0)],"derivedFrom":[subQ1,subQ0]})])]});}
            var Q23;
            {var subQ0=sQuery(id+"F0.wireOp",EDGE,"E10.7.0.0");var subQ1=sQuery(id+"F0.wireOp",EDGE,"E10.6.0.0");Q23=makeQuery(id+"F1.opExtrude","SWEPT_EDGE",EDGE,{"disambiguationData":[OSD([subQ1,subQ0]),TDD([makeQuery(id+"F0.imprint","INTERSECT",VERTEX,{"disambiguationData":[OD(1.0)],"derivedFrom":[subQ1,subQ0]})])]});}
            var Q24;
            {var subQ0=sQuery(id+"F0.wireOp",EDGE,"E10.7.0.0");var subQ1=sQuery(id+"F0.wireOp",EDGE,"E1.right");Q24=makeQuery(id+"F1.opExtrude","SWEPT_EDGE",EDGE,{"disambiguationData":[OSD([subQ1,subQ0]),TDD([makeQuery(id+"F0.imprint","INTERSECT",VERTEX,{"disambiguationData":[OD(1.0)],"derivedFrom":[subQ1,subQ0]})])]});}
            var Q25;
            {var subQ0=sQuery(id+"F0.wireOp",EDGE,"E10.7.0.0");var subQ1=sQuery(id+"F0.wireOp",EDGE,"E1.right");Q25=makeQuery(id+"F1.opExtrude","SWEPT_EDGE",EDGE,{"disambiguationData":[OSD([subQ1,subQ0]),TDD([makeQuery(id+"F0.imprint","INTERSECT",VERTEX,{"disambiguationData":[OD(0.0)],"derivedFrom":[subQ1,subQ0]})])]});}
            var Q26;
            Q26=makeQuery(id+"F4.opExtrude","SWEPT_EDGE",EDGE,{"disambiguationData":[OSD([sQuery(id+"F0.wireOp",EDGE,"E10.7.0.0"),sQuery(id+"F3.wireOp",EDGE,"E30.1.4"),sQuery(id+"F3.wireOp",EDGE,"E30.1.7")])]});
            var Q27;
            Q27=makeQuery(id+"F4.opExtrude","SWEPT_EDGE",EDGE,{"disambiguationData":[OSD([sQuery(id+"F3.wireOp",EDGE,"E30.1.3"),sQuery(id+"F3.wireOp",EDGE,"E30.1.4")])]});
            var Q28;
            Q28=makeQuery(id+"F4.opExtrude","SWEPT_EDGE",EDGE,{"disambiguationData":[OSD([sQuery(id+"F3.wireOp",EDGE,"E30.1.3"),sQuery(id+"F3.wireOp",EDGE,"E30.1.8")])]});
            var Q29;
            Q29=makeQuery(id+"F4.opExtrude","SWEPT_EDGE",EDGE,{"disambiguationData":[OSD([sQuery(id+"F3.wireOp",EDGE,"E30.1.2"),sQuery(id+"F3.wireOp",EDGE,"E30.1.8")])]});
            var Q30;
            Q30=makeQuery(id+"F4.opExtrude","SWEPT_EDGE",EDGE,{"disambiguationData":[OSD([sQuery(id+"F3.wireOp",EDGE,"E30.1.2"),sQuery(id+"F3.wireOp",EDGE,"E30.1.5")])]});
            var Q31;
            Q31=makeQuery(id+"F4.opExtrude","SWEPT_EDGE",EDGE,{"disambiguationData":[OSD([sQuery(id+"F3.wireOp",EDGE,"E30.1.10"),sQuery(id+"F3.wireOp",EDGE,"E30.1.12")])]});
            var Q32;
            Q32=makeQuery(id+"F4.boolean.opBoolean","INTERSECT",EDGE,{"derivedFrom":[makeQuery(id+"F1.opExtrude","SWEPT_FACE",FACE,{"disambiguationData":[OSD([sQuery(id+"F0.wireOp",EDGE,"E1.bottom")])]}),makeQuery(id+"F4.opExtrude","SWEPT_FACE",FACE,{"disambiguationData":[OSD([sQuery(id+"F3.wireOp",EDGE,"E30.1.12")])]})]});
            var Q33;
            Q33=makeQuery(id+"F4.opExtrude","SWEPT_EDGE",EDGE,{"disambiguationData":[OSD([sQuery(id+"F3.wireOp",EDGE,"E30.1.9"),sQuery(id+"F3.wireOp",EDGE,"E30.1.14")])]});
            var Q34;
            Q34=makeQuery(id+"F10.opExtrude","SWEPT_EDGE",EDGE,{"disambiguationData":[OSD([sQuery(id+"F9.wireOp",EDGE,"E56.2"),sQuery(id+"F9.wireOp",EDGE,"E61.0")])]});
            var Q35;
            {var subQ0=sQuery(id+"F0.wireOp",EDGE,"E10.5.0.0");var subQ1=sQuery(id+"F0.wireOp",EDGE,"E10.4.0.0");Q35=makeQuery(id+"F1.opExtrude","SWEPT_EDGE",EDGE,{"disambiguationData":[OSD([subQ1,subQ0]),TDD([makeQuery(id+"F0.imprint","INTERSECT",VERTEX,{"disambiguationData":[OD(0.0)],"derivedFrom":[subQ1,subQ0]})])]});}
            var Q36;
            {var subQ0=sQuery(id+"F9.wireOp",EDGE,"E56.4");var subQ1=sQuery(id+"F0.wireOp",EDGE,"E10.4.0.0");Q36=makeQuery(id+"F10.opExtrude","SWEPT_EDGE",EDGE,{"disambiguationData":[OSD([subQ1,subQ0]),TDD([makeQuery(id+"F9.imprint","INTERSECT",VERTEX,{"derivedFrom":[makeQuery(id+"F1.opExtrude","CAP_EDGE",EDGE,{"disambiguationData":[OSD([subQ1]),TDD([makeQuery(id+"F0.imprint","IMPRINT",EDGE,{"disambiguationData":[TD([[makeQuery(id+"F0.imprint","INTERSECT",VERTEX,{"disambiguationData":[OD(0.0)],"derivedFrom":[sQuery(id+"F0.wireOp",EDGE,"E10.3.0.0"),subQ1]}),1.0]])],"derivedFrom":subQ1})])],"isStart":false}),subQ0]})])]});}
            var Q37;
            Q37=makeQuery(id+"F10.opExtrude","SWEPT_EDGE",EDGE,{"disambiguationData":[OSD([sQuery(id+"F0.wireOp",EDGE,"E10.4.0.0"),sQuery(id+"F9.wireOp",EDGE,"E57.3")])]});
            var Q38;
            {var subQ0=sQuery(id+"F0.wireOp",EDGE,"E10.4.0.0");var subQ1=sQuery(id+"F0.wireOp",EDGE,"E10.3.0.0");Q38=makeQuery(id+"F1.opExtrude","SWEPT_EDGE",EDGE,{"disambiguationData":[OSD([subQ1,subQ0]),TDD([makeQuery(id+"F0.imprint","INTERSECT",VERTEX,{"disambiguationData":[OD(0.0)],"derivedFrom":[subQ1,subQ0]})])]});}
            var Q39;
            Q39=makeQuery(id+"F6.opExtrude","SWEPT_EDGE",EDGE,{"disambiguationData":[OSD([sQuery(id+"F0.wireOp",EDGE,"E10.3.0.0"),sQuery(id+"F5.wireOp",EDGE,"E31"),sQuery(id+"F5.wireOp",EDGE,"E35.0")])]});
            var Q40;
            Q40=makeQuery(id+"F10.opExtrude","SWEPT_EDGE",EDGE,{"disambiguationData":[OSD([sQuery(id+"F9.wireOp",EDGE,"E57.6"),sQuery(id+"F9.wireOp",EDGE,"E57.7")])]});
            var Q41;
            Q41=makeQuery(id+"F6.opExtrude","SWEPT_EDGE",EDGE,{"disambiguationData":[OSD([sQuery(id+"F5.wireOp",EDGE,"E31"),sQuery(id+"F5.wireOp",EDGE,"E32")])]});
            var Q42;
            Q42=makeQuery(id+"F10.opExtrude","SWEPT_EDGE",EDGE,{"disambiguationData":[OSD([sQuery(id+"F9.wireOp",EDGE,"E56.6"),sQuery(id+"F9.wireOp",EDGE,"E56.7")])]});
            var Q43;
            Q43=makeQuery(id+"F10.opExtrude","SWEPT_EDGE",EDGE,{"disambiguationData":[OSD([sQuery(id+"F5.wireOp",EDGE,"E32"),sQuery(id+"F9.wireOp",EDGE,"E56.6")])]});
            var Q44;
            Q44=makeQuery(id+"F12.boolean.opBoolean","COPY",EDGE,{"derivedFrom":makeQuery(id+"F12.opExtrude","SWEPT_EDGE",EDGE,{"disambiguationData":[OSD([sQuery(id+"F11.wireOp",EDGE,"E67"),sQuery(id+"F11.wireOp",EDGE,"E68")])]})});
            var Q45;
            Q45=makeQuery(id+"F12.boolean.opBoolean","COPY",EDGE,{"derivedFrom":makeQuery(id+"F12.opExtrude","SWEPT_EDGE",EDGE,{"disambiguationData":[OSD([sQuery(id+"F11.wireOp",EDGE,"E69"),sQuery(id+"F11.wireOp",EDGE,"E70")])]})});
            var Q46;
            Q46=makeQuery(id+"F12.boolean.opBoolean","COPY",EDGE,{"derivedFrom":makeQuery(id+"F12.opExtrude","SWEPT_EDGE",EDGE,{"disambiguationData":[OSD([sQuery(id+"F11.wireOp",EDGE,"E70"),sQuery(id+"F11.wireOp",EDGE,"E71")])]})});
            var Q47;
            Q47=makeQuery(id+"F12.boolean.opBoolean","COPY",EDGE,{"derivedFrom":makeQuery(id+"F12.opExtrude","SWEPT_EDGE",EDGE,{"disambiguationData":[OSD([sQuery(id+"F11.wireOp",EDGE,"E71"),sQuery(id+"F11.wireOp",EDGE,"E72")])]})});
            var Q48;
            Q48=makeQuery(id+"F12.boolean.opBoolean","COPY",EDGE,{"derivedFrom":makeQuery(id+"F12.opExtrude","SWEPT_EDGE",EDGE,{"disambiguationData":[OSD([sQuery(id+"F11.wireOp",EDGE,"E72"),sQuery(id+"F11.wireOp",EDGE,"E73")])]})});
            var Q49;
            Q49=makeQuery(id+"F12.boolean.opBoolean","COPY",EDGE,{"derivedFrom":makeQuery(id+"F12.opExtrude","SWEPT_EDGE",EDGE,{"disambiguationData":[OSD([sQuery(id+"F11.wireOp",EDGE,"E64"),sQuery(id+"F11.wireOp",EDGE,"E73")])]})});
            var Q50;
            Q50=makeQuery(id+"F12.boolean.opBoolean","COPY",EDGE,{"derivedFrom":makeQuery(id+"F12.opExtrude","SWEPT_EDGE",EDGE,{"disambiguationData":[OSD([sQuery(id+"F11.wireOp",EDGE,"E64"),sQuery(id+"F11.wireOp",EDGE,"E65")])]})});
            var Q51;
            Q51=makeQuery(id+"F12.boolean.opBoolean","COPY",EDGE,{"derivedFrom":makeQuery(id+"F12.opExtrude","SWEPT_EDGE",EDGE,{"disambiguationData":[OSD([sQuery(id+"F11.wireOp",EDGE,"E65"),sQuery(id+"F11.wireOp",EDGE,"E66")])]})});
            var Q52;
            Q52=makeQuery(id+"F12.boolean.opBoolean","COPY",EDGE,{"derivedFrom":makeQuery(id+"F12.opExtrude","SWEPT_EDGE",EDGE,{"disambiguationData":[OSD([sQuery(id+"F11.wireOp",EDGE,"E66"),sQuery(id+"F11.wireOp",EDGE,"E67")])]})});
            var Q53;
            Q53=makeQuery(id+"F12.boolean.opBoolean","COPY",EDGE,{"derivedFrom":makeQuery(id+"F12.opExtrude","SWEPT_EDGE",EDGE,{"disambiguationData":[OSD([sQuery(id+"F11.wireOp",EDGE,"E68"),sQuery(id+"F11.wireOp",EDGE,"E69")])]})});
            fillet(context, id + "F21", {"entities" : qUnion([Q0, Q1, Q2, Q3, Q4, Q5, Q6, Q7, Q8, Q9, Q10, Q11, Q12, Q13, Q14, Q15, Q16, Q17, Q18, Q19, Q20, Q21, Q22, Q23, Q24, Q25, Q26, Q27, Q28, Q29, Q30, Q31, Q32, Q33, Q34, Q35, Q36, Q37, Q38, Q39, Q40, Q41, Q42, Q43, Q44, Q45, Q46, Q47, Q48, Q49, Q50, Q51, Q52, Q53]), "radius" : 1.59 * mm, "tangentPropagation" : true, "allowEdgeOverflow" : false});
        }
    });
